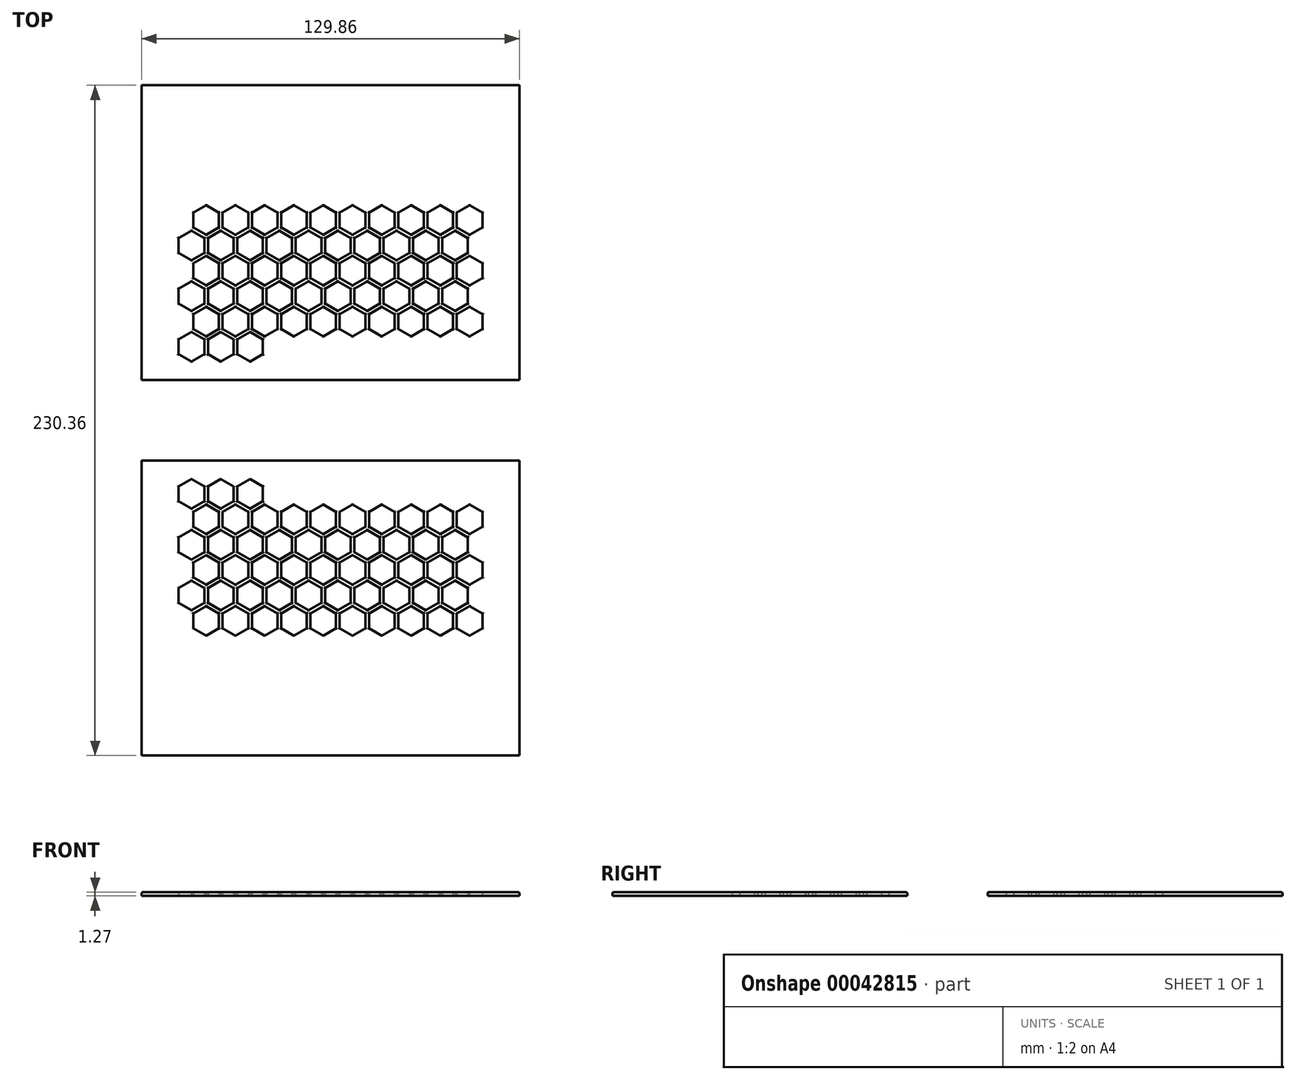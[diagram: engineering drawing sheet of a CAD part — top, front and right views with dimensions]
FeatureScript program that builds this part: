
annotation { "Feature Type Name" : "Feature", "Feature Type Description" : "" }
export const myFeature = defineFeature(function(context is Context, id is Id, definition is map)
    precondition{}
    {
        {
            var Q0;
            Q0=qCreatedBy(makeId("Top.planeOp"),FACE);
            var sketch = newSketch(context, id + "F0", { "sketchPlane" : qUnion([Q0])});
            skCircle(sketch, "E0.cCircle", {"center": v(-4.27, 25.27) * mm, "radius": 5.08 * mm, "construction": true});
            skLineSegment(sketch, "E0.0", {"start": v(-4.27, 20.19) * mm, "end": v(-8.67, 22.73) * mm});
            skLineSegment(sketch, "E0.1", {"start": v(-8.67, 22.73) * mm, "end": v(-8.67, 27.8) * mm});
            skLineSegment(sketch, "E0.2", {"start": v(-8.67, 27.8) * mm, "end": v(-4.27, 30.35) * mm});
            skLineSegment(sketch, "E0.3", {"start": v(-4.27, 30.35) * mm, "end": v(0.13, 27.8) * mm});
            skLineSegment(sketch, "E0.4", {"start": v(0.13, 27.8) * mm, "end": v(0.13, 22.73) * mm});
            skLineSegment(sketch, "E0.5", {"start": v(0.13, 22.73) * mm, "end": v(-4.27, 20.19) * mm});
            skLineSegment(sketch, "E1.1.0.0", {"start": v(5.8, 20.19) * mm, "end": v(1.4, 22.73) * mm});
            skLineSegment(sketch, "E1.1.0.1", {"start": v(1.4, 22.73) * mm, "end": v(1.4, 27.8) * mm});
            skLineSegment(sketch, "E1.1.0.2", {"start": v(1.4, 27.8) * mm, "end": v(5.8, 30.35) * mm});
            skLineSegment(sketch, "E1.1.0.3", {"start": v(5.8, 30.35) * mm, "end": v(10.2, 27.8) * mm});
            skLineSegment(sketch, "E1.1.0.4", {"start": v(10.2, 27.8) * mm, "end": v(10.2, 22.73) * mm});
            skLineSegment(sketch, "E1.1.0.5", {"start": v(10.2, 22.73) * mm, "end": v(5.8, 20.19) * mm});
            skCircle(sketch, "E1.1.0.6", {"center": v(5.8, 25.27) * mm, "radius": 5.08 * mm, "construction": true});
            skLineSegment(sketch, "E1.2.0.0", {"start": v(15.87, 20.19) * mm, "end": v(11.47, 22.73) * mm});
            skLineSegment(sketch, "E1.2.0.1", {"start": v(11.47, 22.73) * mm, "end": v(11.47, 27.8) * mm});
            skLineSegment(sketch, "E1.2.0.2", {"start": v(11.47, 27.8) * mm, "end": v(15.87, 30.35) * mm});
            skLineSegment(sketch, "E1.2.0.3", {"start": v(15.87, 30.35) * mm, "end": v(20.27, 27.8) * mm});
            skLineSegment(sketch, "E1.2.0.4", {"start": v(20.27, 27.8) * mm, "end": v(20.27, 22.73) * mm});
            skLineSegment(sketch, "E1.2.0.5", {"start": v(20.27, 22.73) * mm, "end": v(15.87, 20.19) * mm});
            skCircle(sketch, "E1.2.0.6", {"center": v(15.87, 25.27) * mm, "radius": 5.08 * mm, "construction": true});
            skLineSegment(sketch, "E1.direction1", {"start": v(-8.67, 22.73) * mm, "end": v(1.4, 22.73) * mm, "construction": true});
            skLineSegment(sketch, "E2.0.1.0", {"start": v(-3.63, 31.45) * mm, "end": v(6.44, 31.45) * mm, "construction": true});
            skLineSegment(sketch, "E2.0.1.1", {"start": v(75.65, 36.53) * mm, "end": v(75.65, 31.45) * mm});
            skLineSegment(sketch, "E2.0.1.2", {"start": v(45.44, 31.45) * mm, "end": v(41.04, 28.9) * mm});
            skLineSegment(sketch, "E2.0.1.3", {"start": v(36.64, 31.45) * mm, "end": v(36.64, 36.53) * mm});
            skCircle(sketch, "E2.0.1.4", {"center": v(61.18, 33.99) * mm, "radius": 5.08 * mm, "construction": true});
            skLineSegment(sketch, "E2.0.1.5", {"start": v(86.99, 31.45) * mm, "end": v(86.99, 36.53) * mm});
            skCircle(sketch, "E2.0.1.6", {"center": v(51.11, 33.99) * mm, "radius": 5.08 * mm, "construction": true});
            skLineSegment(sketch, "E2.0.1.7", {"start": v(5.17, 36.53) * mm, "end": v(5.17, 31.45) * mm});
            skLineSegment(sketch, "E2.0.1.8", {"start": v(46.71, 36.53) * mm, "end": v(51.11, 39.07) * mm});
            skLineSegment(sketch, "E2.0.1.9", {"start": v(61.18, 28.9) * mm, "end": v(56.78, 31.45) * mm});
            skLineSegment(sketch, "E2.0.1.10", {"start": v(26.58, 36.53) * mm, "end": v(30.98, 39.07) * mm});
            skLineSegment(sketch, "E2.0.1.11", {"start": v(55.51, 36.53) * mm, "end": v(55.51, 31.45) * mm});
            skLineSegment(sketch, "E2.0.1.12", {"start": v(81.32, 28.9) * mm, "end": v(76.92, 31.45) * mm});
            skCircle(sketch, "E2.0.1.13", {"center": v(71.25, 33.99) * mm, "radius": 5.08 * mm, "construction": true});
            skLineSegment(sketch, "E2.0.1.14", {"start": v(41.04, 28.9) * mm, "end": v(36.64, 31.45) * mm});
            skLineSegment(sketch, "E2.0.1.15", {"start": v(25.3, 31.45) * mm, "end": v(20.9, 28.9) * mm});
            skLineSegment(sketch, "E2.0.1.16", {"start": v(35.37, 36.53) * mm, "end": v(35.37, 31.45) * mm});
            skLineSegment(sketch, "E2.0.1.17", {"start": v(6.44, 36.53) * mm, "end": v(10.84, 39.07) * mm});
            skLineSegment(sketch, "E2.0.1.18", {"start": v(0.77, 28.9) * mm, "end": v(-3.63, 31.45) * mm});
            skLineSegment(sketch, "E2.0.1.19", {"start": v(41.04, 39.07) * mm, "end": v(45.44, 36.53) * mm});
            skCircle(sketch, "E2.0.1.20", {"center": v(20.9, 33.99) * mm, "radius": 5.08 * mm, "construction": true});
            skLineSegment(sketch, "E2.0.1.21", {"start": v(-3.63, 31.45) * mm, "end": v(-3.63, 36.53) * mm});
            skLineSegment(sketch, "E2.0.1.22", {"start": v(0.77, 39.07) * mm, "end": v(5.17, 36.53) * mm});
            skLineSegment(sketch, "E2.0.1.23", {"start": v(5.17, 31.45) * mm, "end": v(0.77, 28.9) * mm});
            skLineSegment(sketch, "E2.0.1.24", {"start": v(20.9, 39.07) * mm, "end": v(25.3, 36.53) * mm});
            skLineSegment(sketch, "E2.0.1.25", {"start": v(45.44, 36.53) * mm, "end": v(45.44, 31.45) * mm});
            skLineSegment(sketch, "E2.0.1.26", {"start": v(30.98, 28.9) * mm, "end": v(26.58, 31.45) * mm});
            skCircle(sketch, "E2.0.1.27", {"center": v(0.77, 33.99) * mm, "radius": 5.08 * mm, "construction": true});
            skLineSegment(sketch, "E2.0.1.28", {"start": v(71.25, 39.07) * mm, "end": v(75.65, 36.53) * mm});
            skLineSegment(sketch, "E2.0.1.29", {"start": v(65.58, 31.45) * mm, "end": v(61.18, 28.9) * mm});
            skLineSegment(sketch, "E2.0.1.30", {"start": v(56.78, 31.45) * mm, "end": v(56.78, 36.53) * mm});
            skLineSegment(sketch, "E2.0.1.31", {"start": v(36.64, 36.53) * mm, "end": v(41.04, 39.07) * mm});
            skLineSegment(sketch, "E2.0.1.32", {"start": v(66.85, 31.45) * mm, "end": v(66.85, 36.53) * mm});
            skLineSegment(sketch, "E2.0.1.33", {"start": v(-3.63, 36.53) * mm, "end": v(0.77, 39.07) * mm});
            skCircle(sketch, "E2.0.1.34", {"center": v(10.84, 33.99) * mm, "radius": 5.08 * mm, "construction": true});
            skLineSegment(sketch, "E2.0.1.35", {"start": v(16.5, 36.53) * mm, "end": v(20.9, 39.07) * mm});
            skLineSegment(sketch, "E2.0.1.36", {"start": v(85.72, 31.45) * mm, "end": v(81.32, 28.9) * mm});
            skLineSegment(sketch, "E2.0.1.37", {"start": v(10.84, 39.07) * mm, "end": v(15.24, 36.53) * mm});
            skLineSegment(sketch, "E2.0.1.38", {"start": v(65.58, 36.53) * mm, "end": v(65.58, 31.45) * mm});
            skLineSegment(sketch, "E2.0.1.39", {"start": v(81.32, 39.07) * mm, "end": v(85.72, 36.53) * mm});
            skLineSegment(sketch, "E2.0.1.40", {"start": v(10.84, 28.9) * mm, "end": v(6.44, 31.45) * mm});
            skLineSegment(sketch, "E2.0.1.41", {"start": v(26.58, 31.45) * mm, "end": v(26.58, 36.53) * mm});
            skLineSegment(sketch, "E2.0.1.42", {"start": v(51.11, 39.07) * mm, "end": v(55.51, 36.53) * mm});
            skCircle(sketch, "E2.0.1.43", {"center": v(41.04, 33.99) * mm, "radius": 5.08 * mm, "construction": true});
            skLineSegment(sketch, "E2.0.1.44", {"start": v(56.78, 36.53) * mm, "end": v(61.18, 39.07) * mm});
            skCircle(sketch, "E2.0.1.45", {"center": v(91.39, 33.99) * mm, "radius": 5.08 * mm, "construction": true});
            skLineSegment(sketch, "E2.0.1.46", {"start": v(6.44, 31.45) * mm, "end": v(6.44, 36.53) * mm});
            skLineSegment(sketch, "E2.0.1.47", {"start": v(35.37, 31.45) * mm, "end": v(30.98, 28.9) * mm});
            skLineSegment(sketch, "E2.0.1.48", {"start": v(16.5, 31.45) * mm, "end": v(16.5, 36.53) * mm});
            skLineSegment(sketch, "E2.0.1.49", {"start": v(91.39, 28.9) * mm, "end": v(86.99, 31.45) * mm});
            skCircle(sketch, "E2.0.1.50", {"center": v(30.98, 33.99) * mm, "radius": 5.08 * mm, "construction": true});
            skLineSegment(sketch, "E2.0.1.51", {"start": v(91.39, 39.07) * mm, "end": v(95.79, 36.53) * mm});
            skLineSegment(sketch, "E2.0.1.52", {"start": v(95.79, 31.45) * mm, "end": v(91.39, 28.9) * mm});
            skLineSegment(sketch, "E2.0.1.53", {"start": v(86.99, 36.53) * mm, "end": v(91.39, 39.07) * mm});
            skLineSegment(sketch, "E2.0.1.54", {"start": v(95.79, 36.53) * mm, "end": v(95.79, 31.45) * mm});
            skLineSegment(sketch, "E2.0.1.55", {"start": v(55.51, 31.45) * mm, "end": v(51.11, 28.9) * mm});
            skLineSegment(sketch, "E2.0.1.56", {"start": v(30.98, 39.07) * mm, "end": v(35.37, 36.53) * mm});
            skLineSegment(sketch, "E2.0.1.57", {"start": v(25.3, 36.53) * mm, "end": v(25.3, 31.45) * mm});
            skLineSegment(sketch, "E2.0.1.58", {"start": v(76.92, 31.45) * mm, "end": v(76.92, 36.53) * mm});
            skCircle(sketch, "E2.0.1.59", {"center": v(81.32, 33.99) * mm, "radius": 5.08 * mm, "construction": true});
            skLineSegment(sketch, "E2.0.1.60", {"start": v(85.72, 36.53) * mm, "end": v(85.72, 31.45) * mm});
            skLineSegment(sketch, "E2.0.1.61", {"start": v(71.25, 28.9) * mm, "end": v(66.85, 31.45) * mm});
            skLineSegment(sketch, "E2.0.1.62", {"start": v(61.18, 39.07) * mm, "end": v(65.58, 36.53) * mm});
            skLineSegment(sketch, "E2.0.1.63", {"start": v(66.85, 36.53) * mm, "end": v(71.25, 39.07) * mm});
            skLineSegment(sketch, "E2.0.1.64", {"start": v(15.24, 36.53) * mm, "end": v(15.24, 31.45) * mm});
            skLineSegment(sketch, "E2.0.1.65", {"start": v(15.24, 31.45) * mm, "end": v(10.84, 28.9) * mm});
            skLineSegment(sketch, "E2.0.1.66", {"start": v(51.11, 28.9) * mm, "end": v(46.71, 31.45) * mm});
            skLineSegment(sketch, "E2.0.1.67", {"start": v(46.71, 31.45) * mm, "end": v(46.71, 36.53) * mm});
            skLineSegment(sketch, "E2.0.1.68", {"start": v(76.92, 36.53) * mm, "end": v(81.32, 39.07) * mm});
            skLineSegment(sketch, "E2.0.1.69", {"start": v(20.9, 28.9) * mm, "end": v(16.5, 31.45) * mm});
            skLineSegment(sketch, "E2.0.1.70", {"start": v(75.65, 31.45) * mm, "end": v(71.25, 28.9) * mm});
            skLineSegment(sketch, "E2.direction1", {"start": v(-8.67, 22.73) * mm, "end": v(18.3, 22.73) * mm, "construction": true});
            skLineSegment(sketch, "E2.direction2", {"start": v(-8.67, 22.73) * mm, "end": v(-3.63, 31.45) * mm, "construction": true});
            skLineSegment(sketch, "E3", {"start": v(0.13, 27.8) * mm, "end": v(0.77, 28.9) * mm, "construction": true});
            skLineSegment(sketch, "E4", {"start": v(0.77, 28.9) * mm, "end": v(1.4, 27.8) * mm, "construction": true});
            skLineSegment(sketch, "E5", {"start": v(0.13, 27.8) * mm, "end": v(1.4, 27.8) * mm, "construction": true});
            skLineSegment(sketch, "E6.0.1.0", {"start": v(-3.63, 48.89) * mm, "end": v(6.44, 48.89) * mm, "construction": true});
            skCircle(sketch, "E6.0.1.1", {"center": v(20.9, 51.43) * mm, "radius": 5.08 * mm, "construction": true});
            skLineSegment(sketch, "E6.0.1.2", {"start": v(76.92, 53.97) * mm, "end": v(81.32, 56.5) * mm});
            skCircle(sketch, "E6.0.1.3", {"center": v(61.18, 51.43) * mm, "radius": 5.08 * mm, "construction": true});
            skLineSegment(sketch, "E6.0.1.4", {"start": v(80.68, 45.25) * mm, "end": v(80.68, 40.17) * mm});
            skLineSegment(sketch, "E6.0.1.5", {"start": v(-8.67, 40.17) * mm, "end": v(18.3, 40.17) * mm, "construction": true});
            skCircle(sketch, "E6.0.1.6", {"center": v(51.11, 51.43) * mm, "radius": 5.08 * mm, "construction": true});
            skCircle(sketch, "E6.0.1.7", {"center": v(0.77, 51.43) * mm, "radius": 5.08 * mm, "construction": true});
            skLineSegment(sketch, "E6.0.1.8", {"start": v(61.82, 40.17) * mm, "end": v(61.82, 45.25) * mm});
            skCircle(sketch, "E6.0.1.9", {"center": v(76.28, 42.7) * mm, "radius": 5.08 * mm, "construction": true});
            skLineSegment(sketch, "E6.0.1.10", {"start": v(56.15, 37.63) * mm, "end": v(51.75, 40.17) * mm});
            skLineSegment(sketch, "E6.0.1.11", {"start": v(15.87, 37.63) * mm, "end": v(11.47, 40.17) * mm});
            skLineSegment(sketch, "E6.0.1.12", {"start": v(71.25, 56.5) * mm, "end": v(75.65, 53.97) * mm});
            skLineSegment(sketch, "E6.0.1.13", {"start": v(20.27, 40.17) * mm, "end": v(15.87, 37.63) * mm});
            skLineSegment(sketch, "E6.0.1.14", {"start": v(56.78, 53.97) * mm, "end": v(61.18, 56.5) * mm});
            skLineSegment(sketch, "E6.0.1.15", {"start": v(95.79, 48.89) * mm, "end": v(91.39, 46.35) * mm});
            skLineSegment(sketch, "E6.0.1.16", {"start": v(30.34, 40.17) * mm, "end": v(25.94, 37.63) * mm});
            skLineSegment(sketch, "E6.0.1.17", {"start": v(60.55, 45.25) * mm, "end": v(60.55, 40.17) * mm});
            skLineSegment(sketch, "E6.0.1.18", {"start": v(91.39, 56.5) * mm, "end": v(95.79, 53.97) * mm});
            skLineSegment(sketch, "E6.0.1.19", {"start": v(-8.67, 40.17) * mm, "end": v(-3.63, 48.89) * mm, "construction": true});
            skLineSegment(sketch, "E6.0.1.20", {"start": v(41.04, 56.5) * mm, "end": v(45.44, 53.97) * mm});
            skLineSegment(sketch, "E6.0.1.21", {"start": v(36, 37.63) * mm, "end": v(31.61, 40.17) * mm});
            skLineSegment(sketch, "E6.0.1.22", {"start": v(81.32, 56.5) * mm, "end": v(85.72, 53.97) * mm});
            skLineSegment(sketch, "E6.0.1.23", {"start": v(66.22, 37.63) * mm, "end": v(61.82, 40.17) * mm});
            skLineSegment(sketch, "E6.0.1.24", {"start": v(40.4, 40.17) * mm, "end": v(36, 37.63) * mm});
            skLineSegment(sketch, "E6.0.1.25", {"start": v(10.84, 56.5) * mm, "end": v(15.24, 53.97) * mm});
            skLineSegment(sketch, "E6.0.1.26", {"start": v(55.51, 53.97) * mm, "end": v(55.51, 48.89) * mm});
            skLineSegment(sketch, "E6.0.1.27", {"start": v(61.18, 46.35) * mm, "end": v(56.78, 48.89) * mm});
            skLineSegment(sketch, "E6.0.1.28", {"start": v(60.55, 40.17) * mm, "end": v(56.15, 37.63) * mm});
            skLineSegment(sketch, "E6.0.1.29", {"start": v(10.2, 40.17) * mm, "end": v(5.8, 37.63) * mm});
            skLineSegment(sketch, "E6.0.1.30", {"start": v(0.13, 40.17) * mm, "end": v(-4.27, 37.63) * mm});
            skLineSegment(sketch, "E6.0.1.31", {"start": v(45.44, 53.97) * mm, "end": v(45.44, 48.89) * mm});
            skCircle(sketch, "E6.0.1.32", {"center": v(10.84, 51.43) * mm, "radius": 5.08 * mm, "construction": true});
            skLineSegment(sketch, "E6.0.1.33", {"start": v(65.58, 53.97) * mm, "end": v(65.58, 48.89) * mm});
            skLineSegment(sketch, "E6.0.1.34", {"start": v(-3.63, 48.89) * mm, "end": v(-3.63, 53.97) * mm});
            skCircle(sketch, "E6.0.1.35", {"center": v(71.25, 51.43) * mm, "radius": 5.08 * mm, "construction": true});
            skLineSegment(sketch, "E6.0.1.36", {"start": v(90.75, 45.25) * mm, "end": v(90.75, 40.17) * mm});
            skLineSegment(sketch, "E6.0.1.37", {"start": v(61.82, 45.25) * mm, "end": v(66.22, 47.79) * mm});
            skLineSegment(sketch, "E6.0.1.38", {"start": v(46.08, 37.63) * mm, "end": v(41.68, 40.17) * mm});
            skLineSegment(sketch, "E6.0.1.39", {"start": v(71.25, 46.35) * mm, "end": v(66.85, 48.89) * mm});
            skCircle(sketch, "E6.0.1.40", {"center": v(91.39, 51.43) * mm, "radius": 5.08 * mm, "construction": true});
            skLineSegment(sketch, "E6.0.1.41", {"start": v(65.58, 48.89) * mm, "end": v(61.18, 46.35) * mm});
            skLineSegment(sketch, "E6.0.1.42", {"start": v(20.9, 56.5) * mm, "end": v(25.3, 53.97) * mm});
            skLineSegment(sketch, "E6.0.1.43", {"start": v(56.15, 47.79) * mm, "end": v(60.55, 45.25) * mm});
            skLineSegment(sketch, "E6.0.1.44", {"start": v(-8.67, 45.25) * mm, "end": v(-4.27, 47.79) * mm});
            skCircle(sketch, "E6.0.1.45", {"center": v(25.94, 42.7) * mm, "radius": 5.08 * mm, "construction": true});
            skLineSegment(sketch, "E6.0.1.46", {"start": v(90.75, 40.17) * mm, "end": v(86.35, 37.63) * mm});
            skCircle(sketch, "E6.0.1.47", {"center": v(-4.27, 42.7) * mm, "radius": 5.08 * mm, "construction": true});
            skLineSegment(sketch, "E6.0.1.48", {"start": v(51.11, 56.5) * mm, "end": v(55.51, 53.97) * mm});
            skLineSegment(sketch, "E6.0.1.49", {"start": v(80.68, 40.17) * mm, "end": v(76.28, 37.63) * mm});
            skCircle(sketch, "E6.0.1.50", {"center": v(5.8, 42.7) * mm, "radius": 5.08 * mm, "construction": true});
            skLineSegment(sketch, "E6.0.1.51", {"start": v(0.77, 56.5) * mm, "end": v(5.17, 53.97) * mm});
            skLineSegment(sketch, "E6.0.1.52", {"start": v(66.22, 47.79) * mm, "end": v(70.62, 45.25) * mm});
            skLineSegment(sketch, "E6.0.1.53", {"start": v(61.18, 56.5) * mm, "end": v(65.58, 53.97) * mm});
            skLineSegment(sketch, "E6.0.1.54", {"start": v(56.78, 48.89) * mm, "end": v(56.78, 53.97) * mm});
            skLineSegment(sketch, "E6.0.1.55", {"start": v(81.95, 40.17) * mm, "end": v(81.95, 45.25) * mm});
            skCircle(sketch, "E6.0.1.56", {"center": v(56.15, 42.7) * mm, "radius": 5.08 * mm, "construction": true});
            skLineSegment(sketch, "E6.0.1.57", {"start": v(86.99, 53.97) * mm, "end": v(91.39, 56.5) * mm});
            skCircle(sketch, "E6.0.1.58", {"center": v(81.32, 51.43) * mm, "radius": 5.08 * mm, "construction": true});
            skLineSegment(sketch, "E6.0.1.59", {"start": v(-4.27, 37.63) * mm, "end": v(-8.67, 40.17) * mm});
            skLineSegment(sketch, "E6.0.1.60", {"start": v(25.94, 37.63) * mm, "end": v(21.54, 40.17) * mm});
            skCircle(sketch, "E6.0.1.61", {"center": v(86.35, 42.7) * mm, "radius": 5.08 * mm, "construction": true});
            skLineSegment(sketch, "E6.0.1.62", {"start": v(41.68, 45.25) * mm, "end": v(46.08, 47.79) * mm});
            skLineSegment(sketch, "E6.0.1.63", {"start": v(66.85, 53.97) * mm, "end": v(71.25, 56.5) * mm});
            skLineSegment(sketch, "E6.0.1.64", {"start": v(36.64, 53.97) * mm, "end": v(41.04, 56.5) * mm});
            skLineSegment(sketch, "E6.0.1.65", {"start": v(70.62, 40.17) * mm, "end": v(66.22, 37.63) * mm});
            skLineSegment(sketch, "E6.0.1.66", {"start": v(16.5, 48.89) * mm, "end": v(16.5, 53.97) * mm});
            skLineSegment(sketch, "E6.0.1.67", {"start": v(66.85, 48.89) * mm, "end": v(66.85, 53.97) * mm});
            skLineSegment(sketch, "E6.0.1.68", {"start": v(15.24, 53.97) * mm, "end": v(15.24, 48.89) * mm});
            skCircle(sketch, "E6.0.1.69", {"center": v(66.22, 42.7) * mm, "radius": 5.08 * mm, "construction": true});
            skLineSegment(sketch, "E6.0.1.70", {"start": v(50.48, 45.25) * mm, "end": v(50.48, 40.17) * mm});
            skLineSegment(sketch, "E6.0.1.71", {"start": v(-3.63, 53.97) * mm, "end": v(0.77, 56.5) * mm});
            skLineSegment(sketch, "E6.0.1.72", {"start": v(6.44, 53.97) * mm, "end": v(10.84, 56.5) * mm});
            skLineSegment(sketch, "E6.0.1.73", {"start": v(-8.67, 40.17) * mm, "end": v(-8.67, 45.25) * mm});
            skCircle(sketch, "E6.0.1.74", {"center": v(41.04, 51.43) * mm, "radius": 5.08 * mm, "construction": true});
            skLineSegment(sketch, "E6.0.1.75", {"start": v(46.71, 48.89) * mm, "end": v(46.71, 53.97) * mm});
            skLineSegment(sketch, "E6.0.1.76", {"start": v(16.5, 53.97) * mm, "end": v(20.9, 56.5) * mm});
            skLineSegment(sketch, "E6.0.1.77", {"start": v(5.8, 37.63) * mm, "end": v(1.4, 40.17) * mm});
            skLineSegment(sketch, "E6.0.1.78", {"start": v(30.98, 56.5) * mm, "end": v(35.37, 53.97) * mm});
            skCircle(sketch, "E6.0.1.79", {"center": v(46.08, 42.7) * mm, "radius": 5.08 * mm, "construction": true});
            skLineSegment(sketch, "E6.0.1.80", {"start": v(86.35, 37.63) * mm, "end": v(81.95, 40.17) * mm});
            skLineSegment(sketch, "E6.0.1.81", {"start": v(95.79, 53.97) * mm, "end": v(95.79, 48.89) * mm});
            skLineSegment(sketch, "E6.0.1.82", {"start": v(51.75, 40.17) * mm, "end": v(51.75, 45.25) * mm});
            skLineSegment(sketch, "E6.0.1.83", {"start": v(46.71, 53.97) * mm, "end": v(51.11, 56.5) * mm});
            skCircle(sketch, "E6.0.1.84", {"center": v(30.98, 51.43) * mm, "radius": 5.08 * mm, "construction": true});
            skLineSegment(sketch, "E6.0.1.85", {"start": v(26.58, 53.97) * mm, "end": v(30.98, 56.5) * mm});
            skLineSegment(sketch, "E6.0.1.86", {"start": v(50.48, 40.17) * mm, "end": v(46.08, 37.63) * mm});
            skLineSegment(sketch, "E6.0.1.87", {"start": v(76.28, 37.63) * mm, "end": v(71.89, 40.17) * mm});
            skLineSegment(sketch, "E6.0.1.88", {"start": v(5.17, 53.97) * mm, "end": v(5.17, 48.89) * mm});
            skLineSegment(sketch, "E6.0.1.89", {"start": v(51.11, 46.35) * mm, "end": v(46.71, 48.89) * mm});
            skLineSegment(sketch, "E6.0.1.90", {"start": v(86.35, 47.79) * mm, "end": v(90.75, 45.25) * mm});
            skLineSegment(sketch, "E6.0.1.91", {"start": v(71.89, 40.17) * mm, "end": v(71.89, 45.25) * mm});
            skLineSegment(sketch, "E6.0.1.92", {"start": v(81.32, 46.35) * mm, "end": v(76.92, 48.89) * mm});
            skCircle(sketch, "E6.0.1.93", {"center": v(36, 42.7) * mm, "radius": 5.08 * mm, "construction": true});
            skLineSegment(sketch, "E6.0.1.94", {"start": v(85.72, 53.97) * mm, "end": v(85.72, 48.89) * mm});
            skLineSegment(sketch, "E6.0.1.95", {"start": v(10.84, 46.35) * mm, "end": v(6.44, 48.89) * mm});
            skLineSegment(sketch, "E6.0.1.96", {"start": v(20.27, 45.25) * mm, "end": v(20.27, 40.17) * mm});
            skLineSegment(sketch, "E6.0.1.97", {"start": v(31.61, 40.17) * mm, "end": v(31.61, 45.25) * mm});
            skLineSegment(sketch, "E6.0.1.98", {"start": v(30.34, 45.25) * mm, "end": v(30.34, 40.17) * mm});
            skLineSegment(sketch, "E6.0.1.99", {"start": v(5.17, 48.89) * mm, "end": v(0.77, 46.35) * mm});
            skLineSegment(sketch, "E6.0.1.100", {"start": v(31.61, 45.25) * mm, "end": v(36, 47.79) * mm});
            skLineSegment(sketch, "E6.0.1.101", {"start": v(81.95, 45.25) * mm, "end": v(86.35, 47.79) * mm});
            skLineSegment(sketch, "E6.0.1.102", {"start": v(86.99, 48.89) * mm, "end": v(86.99, 53.97) * mm});
            skLineSegment(sketch, "E6.0.1.103", {"start": v(55.51, 48.89) * mm, "end": v(51.11, 46.35) * mm});
            skLineSegment(sketch, "E6.0.1.104", {"start": v(75.65, 48.89) * mm, "end": v(71.25, 46.35) * mm});
            skLineSegment(sketch, "E6.0.1.105", {"start": v(76.28, 47.79) * mm, "end": v(80.68, 45.25) * mm});
            skLineSegment(sketch, "E6.0.1.106", {"start": v(30.98, 46.35) * mm, "end": v(26.58, 48.89) * mm});
            skLineSegment(sketch, "E6.0.1.107", {"start": v(26.58, 48.89) * mm, "end": v(26.58, 53.97) * mm});
            skLineSegment(sketch, "E6.0.1.108", {"start": v(1.4, 45.25) * mm, "end": v(5.8, 47.79) * mm});
            skLineSegment(sketch, "E6.0.1.109", {"start": v(15.87, 47.79) * mm, "end": v(20.27, 45.25) * mm});
            skLineSegment(sketch, "E6.0.1.110", {"start": v(45.44, 48.89) * mm, "end": v(41.04, 46.35) * mm});
            skLineSegment(sketch, "E6.0.1.111", {"start": v(76.92, 48.89) * mm, "end": v(76.92, 53.97) * mm});
            skLineSegment(sketch, "E6.0.1.112", {"start": v(1.4, 40.17) * mm, "end": v(1.4, 45.25) * mm});
            skLineSegment(sketch, "E6.0.1.113", {"start": v(10.2, 45.25) * mm, "end": v(10.2, 40.17) * mm});
            skLineSegment(sketch, "E6.0.1.114", {"start": v(20.9, 46.35) * mm, "end": v(16.5, 48.89) * mm});
            skLineSegment(sketch, "E6.0.1.115", {"start": v(25.3, 53.97) * mm, "end": v(25.3, 48.89) * mm});
            skCircle(sketch, "E6.0.1.116", {"center": v(15.87, 42.7) * mm, "radius": 5.08 * mm, "construction": true});
            skLineSegment(sketch, "E6.0.1.117", {"start": v(0.13, 45.25) * mm, "end": v(0.13, 40.17) * mm});
            skLineSegment(sketch, "E6.0.1.118", {"start": v(36, 47.79) * mm, "end": v(40.4, 45.25) * mm});
            skLineSegment(sketch, "E6.0.1.119", {"start": v(-8.67, 40.17) * mm, "end": v(1.4, 40.17) * mm, "construction": true});
            skLineSegment(sketch, "E6.0.1.120", {"start": v(41.04, 46.35) * mm, "end": v(36.64, 48.89) * mm});
            skLineSegment(sketch, "E6.0.1.121", {"start": v(11.47, 45.25) * mm, "end": v(15.87, 47.79) * mm});
            skLineSegment(sketch, "E6.0.1.122", {"start": v(41.68, 40.17) * mm, "end": v(41.68, 45.25) * mm});
            skLineSegment(sketch, "E6.0.1.123", {"start": v(6.44, 48.89) * mm, "end": v(6.44, 53.97) * mm});
            skLineSegment(sketch, "E6.0.1.124", {"start": v(51.75, 45.25) * mm, "end": v(56.15, 47.79) * mm});
            skLineSegment(sketch, "E6.0.1.125", {"start": v(40.4, 45.25) * mm, "end": v(40.4, 40.17) * mm});
            skLineSegment(sketch, "E6.0.1.126", {"start": v(25.3, 48.89) * mm, "end": v(20.9, 46.35) * mm});
            skLineSegment(sketch, "E6.0.1.127", {"start": v(70.62, 45.25) * mm, "end": v(70.62, 40.17) * mm});
            skLineSegment(sketch, "E6.0.1.128", {"start": v(35.37, 48.89) * mm, "end": v(30.98, 46.35) * mm});
            skLineSegment(sketch, "E6.0.1.129", {"start": v(46.08, 47.79) * mm, "end": v(50.48, 45.25) * mm});
            skLineSegment(sketch, "E6.0.1.130", {"start": v(21.54, 40.17) * mm, "end": v(21.54, 45.25) * mm});
            skLineSegment(sketch, "E6.0.1.131", {"start": v(35.37, 53.97) * mm, "end": v(35.37, 48.89) * mm});
            skLineSegment(sketch, "E6.0.1.132", {"start": v(85.72, 48.89) * mm, "end": v(81.32, 46.35) * mm});
            skLineSegment(sketch, "E6.0.1.133", {"start": v(71.89, 45.25) * mm, "end": v(76.28, 47.79) * mm});
            skLineSegment(sketch, "E6.0.1.134", {"start": v(21.54, 45.25) * mm, "end": v(25.94, 47.79) * mm});
            skLineSegment(sketch, "E6.0.1.135", {"start": v(91.39, 46.35) * mm, "end": v(86.99, 48.89) * mm});
            skLineSegment(sketch, "E6.0.1.136", {"start": v(75.65, 53.97) * mm, "end": v(75.65, 48.89) * mm});
            skLineSegment(sketch, "E6.0.1.137", {"start": v(15.24, 48.89) * mm, "end": v(10.84, 46.35) * mm});
            skLineSegment(sketch, "E6.0.1.138", {"start": v(36.64, 48.89) * mm, "end": v(36.64, 53.97) * mm});
            skLineSegment(sketch, "E6.0.1.139", {"start": v(5.8, 47.79) * mm, "end": v(10.2, 45.25) * mm});
            skLineSegment(sketch, "E6.0.1.140", {"start": v(25.94, 47.79) * mm, "end": v(30.34, 45.25) * mm});
            skLineSegment(sketch, "E6.0.1.141", {"start": v(11.47, 40.17) * mm, "end": v(11.47, 45.25) * mm});
            skLineSegment(sketch, "E6.0.1.142", {"start": v(0.77, 46.35) * mm, "end": v(1.4, 45.25) * mm, "construction": true});
            skLineSegment(sketch, "E6.0.1.143", {"start": v(-4.27, 47.79) * mm, "end": v(0.13, 45.25) * mm});
            skLineSegment(sketch, "E6.0.1.144", {"start": v(0.77, 46.35) * mm, "end": v(-3.63, 48.89) * mm});
            skLineSegment(sketch, "E6.0.1.145", {"start": v(0.13, 45.25) * mm, "end": v(1.4, 45.25) * mm, "construction": true});
            skLineSegment(sketch, "E6.0.1.146", {"start": v(0.13, 45.25) * mm, "end": v(0.77, 46.35) * mm, "construction": true});
            skLineSegment(sketch, "E6.0.2.0", {"start": v(-3.63, 66.33) * mm, "end": v(6.44, 66.33) * mm, "construction": true});
            skCircle(sketch, "E6.0.2.1", {"center": v(20.9, 68.87) * mm, "radius": 5.08 * mm, "construction": true});
            skLineSegment(sketch, "E6.0.2.2", {"start": v(76.92, 71.4) * mm, "end": v(81.32, 73.95) * mm});
            skCircle(sketch, "E6.0.2.3", {"center": v(61.18, 68.87) * mm, "radius": 5.08 * mm, "construction": true});
            skLineSegment(sketch, "E6.0.2.4", {"start": v(80.68, 62.69) * mm, "end": v(80.68, 57.6) * mm});
            skLineSegment(sketch, "E6.0.2.5", {"start": v(-8.67, 57.6) * mm, "end": v(18.3, 57.6) * mm, "construction": true});
            skCircle(sketch, "E6.0.2.6", {"center": v(51.11, 68.87) * mm, "radius": 5.08 * mm, "construction": true});
            skCircle(sketch, "E6.0.2.7", {"center": v(0.77, 68.87) * mm, "radius": 5.08 * mm, "construction": true});
            skLineSegment(sketch, "E6.0.2.8", {"start": v(61.82, 57.6) * mm, "end": v(61.82, 62.69) * mm});
            skCircle(sketch, "E6.0.2.9", {"center": v(76.28, 60.15) * mm, "radius": 5.08 * mm, "construction": true});
            skLineSegment(sketch, "E6.0.2.10", {"start": v(56.15, 55.07) * mm, "end": v(51.75, 57.6) * mm});
            skLineSegment(sketch, "E6.0.2.11", {"start": v(15.87, 55.07) * mm, "end": v(11.47, 57.6) * mm});
            skLineSegment(sketch, "E6.0.2.12", {"start": v(71.25, 73.95) * mm, "end": v(75.65, 71.4) * mm});
            skLineSegment(sketch, "E6.0.2.13", {"start": v(20.27, 57.6) * mm, "end": v(15.87, 55.07) * mm});
            skLineSegment(sketch, "E6.0.2.14", {"start": v(56.78, 71.4) * mm, "end": v(61.18, 73.95) * mm});
            skLineSegment(sketch, "E6.0.2.15", {"start": v(95.79, 66.33) * mm, "end": v(91.39, 63.79) * mm});
            skLineSegment(sketch, "E6.0.2.16", {"start": v(30.34, 57.6) * mm, "end": v(25.94, 55.07) * mm});
            skLineSegment(sketch, "E6.0.2.17", {"start": v(60.55, 62.69) * mm, "end": v(60.55, 57.6) * mm});
            skLineSegment(sketch, "E6.0.2.18", {"start": v(91.39, 73.95) * mm, "end": v(95.79, 71.4) * mm});
            skLineSegment(sketch, "E6.0.2.19", {"start": v(-8.67, 57.6) * mm, "end": v(-3.63, 66.33) * mm, "construction": true});
            skLineSegment(sketch, "E6.0.2.20", {"start": v(41.04, 73.95) * mm, "end": v(45.44, 71.4) * mm});
            skLineSegment(sketch, "E6.0.2.21", {"start": v(36, 55.07) * mm, "end": v(31.61, 57.6) * mm});
            skLineSegment(sketch, "E6.0.2.22", {"start": v(81.32, 73.95) * mm, "end": v(85.72, 71.4) * mm});
            skLineSegment(sketch, "E6.0.2.23", {"start": v(66.22, 55.07) * mm, "end": v(61.82, 57.6) * mm});
            skLineSegment(sketch, "E6.0.2.24", {"start": v(40.4, 57.6) * mm, "end": v(36, 55.07) * mm});
            skLineSegment(sketch, "E6.0.2.25", {"start": v(10.84, 73.95) * mm, "end": v(15.24, 71.4) * mm});
            skLineSegment(sketch, "E6.0.2.26", {"start": v(55.51, 71.4) * mm, "end": v(55.51, 66.33) * mm});
            skLineSegment(sketch, "E6.0.2.27", {"start": v(61.18, 63.79) * mm, "end": v(56.78, 66.33) * mm});
            skLineSegment(sketch, "E6.0.2.28", {"start": v(60.55, 57.6) * mm, "end": v(56.15, 55.07) * mm});
            skLineSegment(sketch, "E6.0.2.29", {"start": v(10.2, 57.6) * mm, "end": v(5.8, 55.07) * mm});
            skLineSegment(sketch, "E6.0.2.30", {"start": v(0.13, 57.6) * mm, "end": v(-4.27, 55.07) * mm});
            skLineSegment(sketch, "E6.0.2.31", {"start": v(45.44, 71.4) * mm, "end": v(45.44, 66.33) * mm});
            skCircle(sketch, "E6.0.2.32", {"center": v(10.84, 68.87) * mm, "radius": 5.08 * mm, "construction": true});
            skLineSegment(sketch, "E6.0.2.33", {"start": v(65.58, 71.4) * mm, "end": v(65.58, 66.33) * mm});
            skLineSegment(sketch, "E6.0.2.34", {"start": v(-3.63, 66.33) * mm, "end": v(-3.63, 71.4) * mm});
            skCircle(sketch, "E6.0.2.35", {"center": v(71.25, 68.87) * mm, "radius": 5.08 * mm, "construction": true});
            skLineSegment(sketch, "E6.0.2.36", {"start": v(90.75, 62.69) * mm, "end": v(90.75, 57.6) * mm});
            skLineSegment(sketch, "E6.0.2.37", {"start": v(61.82, 62.69) * mm, "end": v(66.22, 65.23) * mm});
            skLineSegment(sketch, "E6.0.2.38", {"start": v(46.08, 55.07) * mm, "end": v(41.68, 57.6) * mm});
            skLineSegment(sketch, "E6.0.2.39", {"start": v(71.25, 63.79) * mm, "end": v(66.85, 66.33) * mm});
            skCircle(sketch, "E6.0.2.40", {"center": v(91.39, 68.87) * mm, "radius": 5.08 * mm, "construction": true});
            skLineSegment(sketch, "E6.0.2.41", {"start": v(65.58, 66.33) * mm, "end": v(61.18, 63.79) * mm});
            skLineSegment(sketch, "E6.0.2.42", {"start": v(20.9, 73.95) * mm, "end": v(25.3, 71.4) * mm});
            skLineSegment(sketch, "E6.0.2.43", {"start": v(56.15, 65.23) * mm, "end": v(60.55, 62.69) * mm});
            skLineSegment(sketch, "E6.0.2.44", {"start": v(-8.67, 62.69) * mm, "end": v(-4.27, 65.23) * mm});
            skCircle(sketch, "E6.0.2.45", {"center": v(25.94, 60.15) * mm, "radius": 5.08 * mm, "construction": true});
            skLineSegment(sketch, "E6.0.2.46", {"start": v(90.75, 57.6) * mm, "end": v(86.35, 55.07) * mm});
            skCircle(sketch, "E6.0.2.47", {"center": v(-4.27, 60.15) * mm, "radius": 5.08 * mm, "construction": true});
            skLineSegment(sketch, "E6.0.2.48", {"start": v(51.11, 73.95) * mm, "end": v(55.51, 71.4) * mm});
            skLineSegment(sketch, "E6.0.2.49", {"start": v(80.68, 57.6) * mm, "end": v(76.28, 55.07) * mm});
            skCircle(sketch, "E6.0.2.50", {"center": v(5.8, 60.15) * mm, "radius": 5.08 * mm, "construction": true});
            skLineSegment(sketch, "E6.0.2.51", {"start": v(0.77, 73.95) * mm, "end": v(5.17, 71.4) * mm});
            skLineSegment(sketch, "E6.0.2.52", {"start": v(66.22, 65.23) * mm, "end": v(70.62, 62.69) * mm});
            skLineSegment(sketch, "E6.0.2.53", {"start": v(61.18, 73.95) * mm, "end": v(65.58, 71.4) * mm});
            skLineSegment(sketch, "E6.0.2.54", {"start": v(56.78, 66.33) * mm, "end": v(56.78, 71.4) * mm});
            skLineSegment(sketch, "E6.0.2.55", {"start": v(81.95, 57.6) * mm, "end": v(81.95, 62.69) * mm});
            skCircle(sketch, "E6.0.2.56", {"center": v(56.15, 60.15) * mm, "radius": 5.08 * mm, "construction": true});
            skLineSegment(sketch, "E6.0.2.57", {"start": v(86.99, 71.4) * mm, "end": v(91.39, 73.95) * mm});
            skCircle(sketch, "E6.0.2.58", {"center": v(81.32, 68.87) * mm, "radius": 5.08 * mm, "construction": true});
            skLineSegment(sketch, "E6.0.2.59", {"start": v(-4.27, 55.07) * mm, "end": v(-8.67, 57.6) * mm});
            skLineSegment(sketch, "E6.0.2.60", {"start": v(25.94, 55.07) * mm, "end": v(21.54, 57.6) * mm});
            skCircle(sketch, "E6.0.2.61", {"center": v(86.35, 60.15) * mm, "radius": 5.08 * mm, "construction": true});
            skLineSegment(sketch, "E6.0.2.62", {"start": v(41.68, 62.69) * mm, "end": v(46.08, 65.23) * mm});
            skLineSegment(sketch, "E6.0.2.63", {"start": v(66.85, 71.4) * mm, "end": v(71.25, 73.95) * mm});
            skLineSegment(sketch, "E6.0.2.64", {"start": v(36.64, 71.4) * mm, "end": v(41.04, 73.95) * mm});
            skLineSegment(sketch, "E6.0.2.65", {"start": v(70.62, 57.6) * mm, "end": v(66.22, 55.07) * mm});
            skLineSegment(sketch, "E6.0.2.66", {"start": v(16.5, 66.33) * mm, "end": v(16.5, 71.4) * mm});
            skLineSegment(sketch, "E6.0.2.67", {"start": v(66.85, 66.33) * mm, "end": v(66.85, 71.4) * mm});
            skLineSegment(sketch, "E6.0.2.68", {"start": v(15.24, 71.4) * mm, "end": v(15.24, 66.33) * mm});
            skCircle(sketch, "E6.0.2.69", {"center": v(66.22, 60.15) * mm, "radius": 5.08 * mm, "construction": true});
            skLineSegment(sketch, "E6.0.2.70", {"start": v(50.48, 62.69) * mm, "end": v(50.48, 57.6) * mm});
            skLineSegment(sketch, "E6.0.2.71", {"start": v(-3.63, 71.4) * mm, "end": v(0.77, 73.95) * mm});
            skLineSegment(sketch, "E6.0.2.72", {"start": v(6.44, 71.4) * mm, "end": v(10.84, 73.95) * mm});
            skLineSegment(sketch, "E6.0.2.73", {"start": v(-8.67, 57.6) * mm, "end": v(-8.67, 62.69) * mm});
            skCircle(sketch, "E6.0.2.74", {"center": v(41.04, 68.87) * mm, "radius": 5.08 * mm, "construction": true});
            skLineSegment(sketch, "E6.0.2.75", {"start": v(46.71, 66.33) * mm, "end": v(46.71, 71.4) * mm});
            skLineSegment(sketch, "E6.0.2.76", {"start": v(16.5, 71.4) * mm, "end": v(20.9, 73.95) * mm});
            skLineSegment(sketch, "E6.0.2.77", {"start": v(5.8, 55.07) * mm, "end": v(1.4, 57.6) * mm});
            skLineSegment(sketch, "E6.0.2.78", {"start": v(30.98, 73.95) * mm, "end": v(35.37, 71.4) * mm});
            skCircle(sketch, "E6.0.2.79", {"center": v(46.08, 60.15) * mm, "radius": 5.08 * mm, "construction": true});
            skLineSegment(sketch, "E6.0.2.80", {"start": v(86.35, 55.07) * mm, "end": v(81.95, 57.6) * mm});
            skLineSegment(sketch, "E6.0.2.81", {"start": v(95.79, 71.4) * mm, "end": v(95.79, 66.33) * mm});
            skLineSegment(sketch, "E6.0.2.82", {"start": v(51.75, 57.6) * mm, "end": v(51.75, 62.69) * mm});
            skLineSegment(sketch, "E6.0.2.83", {"start": v(46.71, 71.4) * mm, "end": v(51.11, 73.95) * mm});
            skCircle(sketch, "E6.0.2.84", {"center": v(30.98, 68.87) * mm, "radius": 5.08 * mm, "construction": true});
            skLineSegment(sketch, "E6.0.2.85", {"start": v(26.58, 71.4) * mm, "end": v(30.98, 73.95) * mm});
            skLineSegment(sketch, "E6.0.2.86", {"start": v(50.48, 57.6) * mm, "end": v(46.08, 55.07) * mm});
            skLineSegment(sketch, "E6.0.2.87", {"start": v(76.28, 55.07) * mm, "end": v(71.89, 57.6) * mm});
            skLineSegment(sketch, "E6.0.2.88", {"start": v(5.17, 71.4) * mm, "end": v(5.17, 66.33) * mm});
            skLineSegment(sketch, "E6.0.2.89", {"start": v(51.11, 63.79) * mm, "end": v(46.71, 66.33) * mm});
            skLineSegment(sketch, "E6.0.2.90", {"start": v(86.35, 65.23) * mm, "end": v(90.75, 62.69) * mm});
            skLineSegment(sketch, "E6.0.2.91", {"start": v(71.89, 57.6) * mm, "end": v(71.89, 62.69) * mm});
            skLineSegment(sketch, "E6.0.2.92", {"start": v(81.32, 63.79) * mm, "end": v(76.92, 66.33) * mm});
            skCircle(sketch, "E6.0.2.93", {"center": v(36, 60.15) * mm, "radius": 5.08 * mm, "construction": true});
            skLineSegment(sketch, "E6.0.2.94", {"start": v(85.72, 71.4) * mm, "end": v(85.72, 66.33) * mm});
            skLineSegment(sketch, "E6.0.2.95", {"start": v(10.84, 63.79) * mm, "end": v(6.44, 66.33) * mm});
            skLineSegment(sketch, "E6.0.2.96", {"start": v(20.27, 62.69) * mm, "end": v(20.27, 57.6) * mm});
            skLineSegment(sketch, "E6.0.2.97", {"start": v(31.61, 57.6) * mm, "end": v(31.61, 62.69) * mm});
            skLineSegment(sketch, "E6.0.2.98", {"start": v(30.34, 62.69) * mm, "end": v(30.34, 57.6) * mm});
            skLineSegment(sketch, "E6.0.2.99", {"start": v(5.17, 66.33) * mm, "end": v(0.77, 63.79) * mm});
            skLineSegment(sketch, "E6.0.2.100", {"start": v(31.61, 62.69) * mm, "end": v(36, 65.23) * mm});
            skLineSegment(sketch, "E6.0.2.101", {"start": v(81.95, 62.69) * mm, "end": v(86.35, 65.23) * mm});
            skLineSegment(sketch, "E6.0.2.102", {"start": v(86.99, 66.33) * mm, "end": v(86.99, 71.4) * mm});
            skLineSegment(sketch, "E6.0.2.103", {"start": v(55.51, 66.33) * mm, "end": v(51.11, 63.79) * mm});
            skLineSegment(sketch, "E6.0.2.104", {"start": v(75.65, 66.33) * mm, "end": v(71.25, 63.79) * mm});
            skLineSegment(sketch, "E6.0.2.105", {"start": v(76.28, 65.23) * mm, "end": v(80.68, 62.69) * mm});
            skLineSegment(sketch, "E6.0.2.106", {"start": v(30.98, 63.79) * mm, "end": v(26.58, 66.33) * mm});
            skLineSegment(sketch, "E6.0.2.107", {"start": v(26.58, 66.33) * mm, "end": v(26.58, 71.4) * mm});
            skLineSegment(sketch, "E6.0.2.108", {"start": v(1.4, 62.69) * mm, "end": v(5.8, 65.23) * mm});
            skLineSegment(sketch, "E6.0.2.109", {"start": v(15.87, 65.23) * mm, "end": v(20.27, 62.69) * mm});
            skLineSegment(sketch, "E6.0.2.110", {"start": v(45.44, 66.33) * mm, "end": v(41.04, 63.79) * mm});
            skLineSegment(sketch, "E6.0.2.111", {"start": v(76.92, 66.33) * mm, "end": v(76.92, 71.4) * mm});
            skLineSegment(sketch, "E6.0.2.112", {"start": v(1.4, 57.6) * mm, "end": v(1.4, 62.69) * mm});
            skLineSegment(sketch, "E6.0.2.113", {"start": v(10.2, 62.69) * mm, "end": v(10.2, 57.6) * mm});
            skLineSegment(sketch, "E6.0.2.114", {"start": v(20.9, 63.79) * mm, "end": v(16.5, 66.33) * mm});
            skLineSegment(sketch, "E6.0.2.115", {"start": v(25.3, 71.4) * mm, "end": v(25.3, 66.33) * mm});
            skCircle(sketch, "E6.0.2.116", {"center": v(15.87, 60.15) * mm, "radius": 5.08 * mm, "construction": true});
            skLineSegment(sketch, "E6.0.2.117", {"start": v(0.13, 62.69) * mm, "end": v(0.13, 57.6) * mm});
            skLineSegment(sketch, "E6.0.2.118", {"start": v(36, 65.23) * mm, "end": v(40.4, 62.69) * mm});
            skLineSegment(sketch, "E6.0.2.119", {"start": v(-8.67, 57.6) * mm, "end": v(1.4, 57.6) * mm, "construction": true});
            skLineSegment(sketch, "E6.0.2.120", {"start": v(41.04, 63.79) * mm, "end": v(36.64, 66.33) * mm});
            skLineSegment(sketch, "E6.0.2.121", {"start": v(11.47, 62.69) * mm, "end": v(15.87, 65.23) * mm});
            skLineSegment(sketch, "E6.0.2.122", {"start": v(41.68, 57.6) * mm, "end": v(41.68, 62.69) * mm});
            skLineSegment(sketch, "E6.0.2.123", {"start": v(6.44, 66.33) * mm, "end": v(6.44, 71.4) * mm});
            skLineSegment(sketch, "E6.0.2.124", {"start": v(51.75, 62.69) * mm, "end": v(56.15, 65.23) * mm});
            skLineSegment(sketch, "E6.0.2.125", {"start": v(40.4, 62.69) * mm, "end": v(40.4, 57.6) * mm});
            skLineSegment(sketch, "E6.0.2.126", {"start": v(25.3, 66.33) * mm, "end": v(20.9, 63.79) * mm});
            skLineSegment(sketch, "E6.0.2.127", {"start": v(70.62, 62.69) * mm, "end": v(70.62, 57.6) * mm});
            skLineSegment(sketch, "E6.0.2.128", {"start": v(35.37, 66.33) * mm, "end": v(30.98, 63.79) * mm});
            skLineSegment(sketch, "E6.0.2.129", {"start": v(46.08, 65.23) * mm, "end": v(50.48, 62.69) * mm});
            skLineSegment(sketch, "E6.0.2.130", {"start": v(21.54, 57.6) * mm, "end": v(21.54, 62.69) * mm});
            skLineSegment(sketch, "E6.0.2.131", {"start": v(35.37, 71.4) * mm, "end": v(35.37, 66.33) * mm});
            skLineSegment(sketch, "E6.0.2.132", {"start": v(85.72, 66.33) * mm, "end": v(81.32, 63.79) * mm});
            skLineSegment(sketch, "E6.0.2.133", {"start": v(71.89, 62.69) * mm, "end": v(76.28, 65.23) * mm});
            skLineSegment(sketch, "E6.0.2.134", {"start": v(21.54, 62.69) * mm, "end": v(25.94, 65.23) * mm});
            skLineSegment(sketch, "E6.0.2.135", {"start": v(91.39, 63.79) * mm, "end": v(86.99, 66.33) * mm});
            skLineSegment(sketch, "E6.0.2.136", {"start": v(75.65, 71.4) * mm, "end": v(75.65, 66.33) * mm});
            skLineSegment(sketch, "E6.0.2.137", {"start": v(15.24, 66.33) * mm, "end": v(10.84, 63.79) * mm});
            skLineSegment(sketch, "E6.0.2.138", {"start": v(36.64, 66.33) * mm, "end": v(36.64, 71.4) * mm});
            skLineSegment(sketch, "E6.0.2.139", {"start": v(5.8, 65.23) * mm, "end": v(10.2, 62.69) * mm});
            skLineSegment(sketch, "E6.0.2.140", {"start": v(25.94, 65.23) * mm, "end": v(30.34, 62.69) * mm});
            skLineSegment(sketch, "E6.0.2.141", {"start": v(11.47, 57.6) * mm, "end": v(11.47, 62.69) * mm});
            skLineSegment(sketch, "E6.0.2.142", {"start": v(0.77, 63.79) * mm, "end": v(1.4, 62.69) * mm, "construction": true});
            skLineSegment(sketch, "E6.0.2.143", {"start": v(-4.27, 65.23) * mm, "end": v(0.13, 62.69) * mm});
            skLineSegment(sketch, "E6.0.2.144", {"start": v(0.77, 63.79) * mm, "end": v(-3.63, 66.33) * mm});
            skLineSegment(sketch, "E6.0.2.145", {"start": v(0.13, 62.69) * mm, "end": v(1.4, 62.69) * mm, "construction": true});
            skLineSegment(sketch, "E6.0.2.146", {"start": v(0.13, 62.69) * mm, "end": v(0.77, 63.79) * mm, "construction": true});
            skLineSegment(sketch, "E6.direction1", {"start": v(-3.63, 31.45) * mm, "end": v(21.77, 31.45) * mm, "construction": true});
            skLineSegment(sketch, "E6.direction2", {"start": v(-3.63, 31.45) * mm, "end": v(-3.63, 48.89) * mm, "construction": true});
            skLineSegment(sketch, "E7", {"start": v(5.8, 37.63) * mm, "end": v(5.17, 36.53) * mm, "construction": true});
            skLineSegment(sketch, "E8", {"start": v(5.8, 37.63) * mm, "end": v(6.44, 36.53) * mm, "construction": true});
            skLineSegment(sketch, "E9", {"start": v(5.17, 36.53) * mm, "end": v(6.44, 36.53) * mm, "construction": true});
            skLineSegment(sketch, "E10.bottom", {"start": v(-21.37, 115.18) * mm, "end": v(108.49, 115.18) * mm});
            skLineSegment(sketch, "E10.top", {"start": v(-21.37, 13.84) * mm, "end": v(108.49, 13.84) * mm});
            skLineSegment(sketch, "E10.left", {"start": v(-21.37, 115.18) * mm, "end": v(-21.37, 13.84) * mm});
            skLineSegment(sketch, "E10.right", {"start": v(108.49, 115.18) * mm, "end": v(108.49, 13.84) * mm});
            skLineSegment(sketch, "E11", {"start": v(0, 0) * mm, "end": v(59.74, 0) * mm, "construction": true});
            skSolve(sketch);
        }
        {
            var Q0;
            Q0=qSketchRegion(id+"F0",true);
            extrude(context, id + "F1", {"entities" : qUnion([Q0]), "depth" : 1.27 * mm});
        }
        {
            var Q0;
            Q0=makeQuery(id+"F1.opExtrude","CAP_FACE",FACE,{"disambiguationData":[OSD([sQuery(id+"F0.wireOp",EDGE,"E0.0"),sQuery(id+"F0.wireOp",EDGE,"E0.1"),sQuery(id+"F0.wireOp",EDGE,"E0.2"),sQuery(id+"F0.wireOp",EDGE,"E0.3"),sQuery(id+"F0.wireOp",EDGE,"E0.4"),sQuery(id+"F0.wireOp",EDGE,"E0.5"),sQuery(id+"F0.wireOp",EDGE,"E1.1.0.0"),sQuery(id+"F0.wireOp",EDGE,"E1.1.0.1"),sQuery(id+"F0.wireOp",EDGE,"E1.1.0.2"),sQuery(id+"F0.wireOp",EDGE,"E1.1.0.3"),sQuery(id+"F0.wireOp",EDGE,"E1.1.0.4"),sQuery(id+"F0.wireOp",EDGE,"E1.1.0.5"),sQuery(id+"F0.wireOp",EDGE,"E1.2.0.0"),sQuery(id+"F0.wireOp",EDGE,"E1.2.0.1"),sQuery(id+"F0.wireOp",EDGE,"E1.2.0.2"),sQuery(id+"F0.wireOp",EDGE,"E1.2.0.3"),sQuery(id+"F0.wireOp",EDGE,"E1.2.0.4"),sQuery(id+"F0.wireOp",EDGE,"E1.2.0.5"),sQuery(id+"F0.wireOp",EDGE,"0f33f7c7-d985-4434-8b08-4c21ebd6a896.0.3.0"),sQuery(id+"F0.wireOp",EDGE,"0f33f7c7-d985-4434-8b08-4c21ebd6a896.3.3.0"),sQuery(id+"F0.wireOp",EDGE,"0f33f7c7-d985-4434-8b08-4c21ebd6a896.6.3.0"),sQuery(id+"F0.wireOp",EDGE,"0f33f7c7-d985-4434-8b08-4c21ebd6a896.9.3.0"),sQuery(id+"F0.wireOp",EDGE,"0f33f7c7-d985-4434-8b08-4c21ebd6a896.12.3.0"),sQuery(id+"F0.wireOp",EDGE,"0f33f7c7-d985-4434-8b08-4c21ebd6a896.15.3.0"),sQuery(id+"F0.wireOp",EDGE,"0f33f7c7-d985-4434-8b08-4c21ebd6a896.0.4.0"),sQuery(id+"F0.wireOp",EDGE,"0f33f7c7-d985-4434-8b08-4c21ebd6a896.3.4.0"),sQuery(id+"F0.wireOp",EDGE,"0f33f7c7-d985-4434-8b08-4c21ebd6a896.6.4.0"),sQuery(id+"F0.wireOp",EDGE,"0f33f7c7-d985-4434-8b08-4c21ebd6a896.9.4.0"),sQuery(id+"F0.wireOp",EDGE,"0f33f7c7-d985-4434-8b08-4c21ebd6a896.12.4.0"),sQuery(id+"F0.wireOp",EDGE,"0f33f7c7-d985-4434-8b08-4c21ebd6a896.15.4.0"),sQuery(id+"F0.wireOp",EDGE,"0f33f7c7-d985-4434-8b08-4c21ebd6a896.0.5.0"),sQuery(id+"F0.wireOp",EDGE,"0f33f7c7-d985-4434-8b08-4c21ebd6a896.3.5.0"),sQuery(id+"F0.wireOp",EDGE,"0f33f7c7-d985-4434-8b08-4c21ebd6a896.6.5.0"),sQuery(id+"F0.wireOp",EDGE,"0f33f7c7-d985-4434-8b08-4c21ebd6a896.9.5.0"),sQuery(id+"F0.wireOp",EDGE,"0f33f7c7-d985-4434-8b08-4c21ebd6a896.12.5.0"),sQuery(id+"F0.wireOp",EDGE,"0f33f7c7-d985-4434-8b08-4c21ebd6a896.15.5.0"),sQuery(id+"F0.wireOp",EDGE,"0f33f7c7-d985-4434-8b08-4c21ebd6a896.0.6.0"),sQuery(id+"F0.wireOp",EDGE,"0f33f7c7-d985-4434-8b08-4c21ebd6a896.3.6.0"),sQuery(id+"F0.wireOp",EDGE,"0f33f7c7-d985-4434-8b08-4c21ebd6a896.6.6.0"),sQuery(id+"F0.wireOp",EDGE,"0f33f7c7-d985-4434-8b08-4c21ebd6a896.9.6.0"),sQuery(id+"F0.wireOp",EDGE,"0f33f7c7-d985-4434-8b08-4c21ebd6a896.12.6.0"),sQuery(id+"F0.wireOp",EDGE,"0f33f7c7-d985-4434-8b08-4c21ebd6a896.15.6.0"),sQuery(id+"F0.wireOp",EDGE,"0f33f7c7-d985-4434-8b08-4c21ebd6a896.0.7.0"),sQuery(id+"F0.wireOp",EDGE,"0f33f7c7-d985-4434-8b08-4c21ebd6a896.3.7.0"),sQuery(id+"F0.wireOp",EDGE,"0f33f7c7-d985-4434-8b08-4c21ebd6a896.6.7.0"),sQuery(id+"F0.wireOp",EDGE,"0f33f7c7-d985-4434-8b08-4c21ebd6a896.9.7.0"),sQuery(id+"F0.wireOp",EDGE,"0f33f7c7-d985-4434-8b08-4c21ebd6a896.12.7.0"),sQuery(id+"F0.wireOp",EDGE,"0f33f7c7-d985-4434-8b08-4c21ebd6a896.15.7.0"),sQuery(id+"F0.wireOp",EDGE,"0f33f7c7-d985-4434-8b08-4c21ebd6a896.0.8.0"),sQuery(id+"F0.wireOp",EDGE,"0f33f7c7-d985-4434-8b08-4c21ebd6a896.3.8.0"),sQuery(id+"F0.wireOp",EDGE,"0f33f7c7-d985-4434-8b08-4c21ebd6a896.6.8.0"),sQuery(id+"F0.wireOp",EDGE,"0f33f7c7-d985-4434-8b08-4c21ebd6a896.9.8.0"),sQuery(id+"F0.wireOp",EDGE,"0f33f7c7-d985-4434-8b08-4c21ebd6a896.12.8.0"),sQuery(id+"F0.wireOp",EDGE,"0f33f7c7-d985-4434-8b08-4c21ebd6a896.15.8.0"),sQuery(id+"F0.wireOp",EDGE,"0f33f7c7-d985-4434-8b08-4c21ebd6a896.0.9.0"),sQuery(id+"F0.wireOp",EDGE,"0f33f7c7-d985-4434-8b08-4c21ebd6a896.3.9.0"),sQuery(id+"F0.wireOp",EDGE,"0f33f7c7-d985-4434-8b08-4c21ebd6a896.6.9.0"),sQuery(id+"F0.wireOp",EDGE,"0f33f7c7-d985-4434-8b08-4c21ebd6a896.9.9.0"),sQuery(id+"F0.wireOp",EDGE,"0f33f7c7-d985-4434-8b08-4c21ebd6a896.12.9.0"),sQuery(id+"F0.wireOp",EDGE,"0f33f7c7-d985-4434-8b08-4c21ebd6a896.15.9.0"),sQuery(id+"F0.wireOp",EDGE,"E2.0.1.1"),sQuery(id+"F0.wireOp",EDGE,"E2.0.1.2"),sQuery(id+"F0.wireOp",EDGE,"E2.0.1.3"),sQuery(id+"F0.wireOp",EDGE,"E2.0.1.5"),sQuery(id+"F0.wireOp",EDGE,"E2.0.1.7"),sQuery(id+"F0.wireOp",EDGE,"E2.0.1.8"),sQuery(id+"F0.wireOp",EDGE,"E2.0.1.9"),sQuery(id+"F0.wireOp",EDGE,"E2.0.1.10"),sQuery(id+"F0.wireOp",EDGE,"E2.0.1.11"),sQuery(id+"F0.wireOp",EDGE,"E2.0.1.12"),sQuery(id+"F0.wireOp",EDGE,"E2.0.1.14"),sQuery(id+"F0.wireOp",EDGE,"E2.0.1.15"),sQuery(id+"F0.wireOp",EDGE,"E2.0.1.16"),sQuery(id+"F0.wireOp",EDGE,"E2.0.1.17"),sQuery(id+"F0.wireOp",EDGE,"E2.0.1.18"),sQuery(id+"F0.wireOp",EDGE,"E2.0.1.19"),sQuery(id+"F0.wireOp",EDGE,"E2.0.1.21"),sQuery(id+"F0.wireOp",EDGE,"E2.0.1.22"),sQuery(id+"F0.wireOp",EDGE,"E2.0.1.23"),sQuery(id+"F0.wireOp",EDGE,"E2.0.1.24"),sQuery(id+"F0.wireOp",EDGE,"E2.0.1.25"),sQuery(id+"F0.wireOp",EDGE,"E2.0.1.26"),sQuery(id+"F0.wireOp",EDGE,"E2.0.1.28"),sQuery(id+"F0.wireOp",EDGE,"E2.0.1.29"),sQuery(id+"F0.wireOp",EDGE,"E2.0.1.30"),sQuery(id+"F0.wireOp",EDGE,"E2.0.1.31"),sQuery(id+"F0.wireOp",EDGE,"E2.0.1.32"),sQuery(id+"F0.wireOp",EDGE,"E2.0.1.33"),sQuery(id+"F0.wireOp",EDGE,"E2.0.1.35"),sQuery(id+"F0.wireOp",EDGE,"E2.0.1.36"),sQuery(id+"F0.wireOp",EDGE,"E2.0.1.37"),sQuery(id+"F0.wireOp",EDGE,"E2.0.1.38"),sQuery(id+"F0.wireOp",EDGE,"E2.0.1.39"),sQuery(id+"F0.wireOp",EDGE,"E2.0.1.40"),sQuery(id+"F0.wireOp",EDGE,"E2.0.1.41"),sQuery(id+"F0.wireOp",EDGE,"E2.0.1.42"),sQuery(id+"F0.wireOp",EDGE,"E2.0.1.44"),sQuery(id+"F0.wireOp",EDGE,"E2.0.1.46"),sQuery(id+"F0.wireOp",EDGE,"E2.0.1.47"),sQuery(id+"F0.wireOp",EDGE,"E2.0.1.48"),sQuery(id+"F0.wireOp",EDGE,"E2.0.1.49"),sQuery(id+"F0.wireOp",EDGE,"E2.0.1.51"),sQuery(id+"F0.wireOp",EDGE,"E2.0.1.52"),sQuery(id+"F0.wireOp",EDGE,"E2.0.1.53"),sQuery(id+"F0.wireOp",EDGE,"E2.0.1.54"),sQuery(id+"F0.wireOp",EDGE,"E2.0.1.55"),sQuery(id+"F0.wireOp",EDGE,"E2.0.1.56"),sQuery(id+"F0.wireOp",EDGE,"E2.0.1.57"),sQuery(id+"F0.wireOp",EDGE,"E2.0.1.58"),sQuery(id+"F0.wireOp",EDGE,"E2.0.1.60"),sQuery(id+"F0.wireOp",EDGE,"E2.0.1.61"),sQuery(id+"F0.wireOp",EDGE,"E2.0.1.62"),sQuery(id+"F0.wireOp",EDGE,"E2.0.1.63"),sQuery(id+"F0.wireOp",EDGE,"E2.0.1.64"),sQuery(id+"F0.wireOp",EDGE,"E2.0.1.65"),sQuery(id+"F0.wireOp",EDGE,"E2.0.1.66"),sQuery(id+"F0.wireOp",EDGE,"E2.0.1.67"),sQuery(id+"F0.wireOp",EDGE,"E2.0.1.68"),sQuery(id+"F0.wireOp",EDGE,"E2.0.1.69"),sQuery(id+"F0.wireOp",EDGE,"E2.0.1.70"),sQuery(id+"F0.wireOp",EDGE,"E6.0.1.2"),sQuery(id+"F0.wireOp",EDGE,"E6.0.1.4"),sQuery(id+"F0.wireOp",EDGE,"E6.0.1.8"),sQuery(id+"F0.wireOp",EDGE,"E6.0.1.10"),sQuery(id+"F0.wireOp",EDGE,"E6.0.1.11"),sQuery(id+"F0.wireOp",EDGE,"E6.0.1.12"),sQuery(id+"F0.wireOp",EDGE,"E6.0.1.13"),sQuery(id+"F0.wireOp",EDGE,"E6.0.1.14"),sQuery(id+"F0.wireOp",EDGE,"E6.0.1.15"),sQuery(id+"F0.wireOp",EDGE,"E6.0.1.16"),sQuery(id+"F0.wireOp",EDGE,"E6.0.1.17"),sQuery(id+"F0.wireOp",EDGE,"E6.0.1.18"),sQuery(id+"F0.wireOp",EDGE,"E6.0.1.20"),sQuery(id+"F0.wireOp",EDGE,"E6.0.1.21"),sQuery(id+"F0.wireOp",EDGE,"E6.0.1.22"),sQuery(id+"F0.wireOp",EDGE,"E6.0.1.23"),sQuery(id+"F0.wireOp",EDGE,"E6.0.1.24"),sQuery(id+"F0.wireOp",EDGE,"E6.0.1.25"),sQuery(id+"F0.wireOp",EDGE,"E6.0.1.26"),sQuery(id+"F0.wireOp",EDGE,"E6.0.1.27"),sQuery(id+"F0.wireOp",EDGE,"E6.0.1.28"),sQuery(id+"F0.wireOp",EDGE,"E6.0.1.29"),sQuery(id+"F0.wireOp",EDGE,"E6.0.1.30"),sQuery(id+"F0.wireOp",EDGE,"E6.0.1.31"),sQuery(id+"F0.wireOp",EDGE,"E6.0.1.33"),sQuery(id+"F0.wireOp",EDGE,"E6.0.1.34"),sQuery(id+"F0.wireOp",EDGE,"E6.0.1.36"),sQuery(id+"F0.wireOp",EDGE,"E6.0.1.37"),sQuery(id+"F0.wireOp",EDGE,"E6.0.1.38"),sQuery(id+"F0.wireOp",EDGE,"E6.0.1.39"),sQuery(id+"F0.wireOp",EDGE,"E6.0.1.41"),sQuery(id+"F0.wireOp",EDGE,"E6.0.1.42"),sQuery(id+"F0.wireOp",EDGE,"E6.0.1.43"),sQuery(id+"F0.wireOp",EDGE,"E6.0.1.44"),sQuery(id+"F0.wireOp",EDGE,"E6.0.1.46"),sQuery(id+"F0.wireOp",EDGE,"E6.0.1.48"),sQuery(id+"F0.wireOp",EDGE,"E6.0.1.49"),sQuery(id+"F0.wireOp",EDGE,"E6.0.1.51"),sQuery(id+"F0.wireOp",EDGE,"E6.0.1.52"),sQuery(id+"F0.wireOp",EDGE,"E6.0.1.53"),sQuery(id+"F0.wireOp",EDGE,"E6.0.1.54"),sQuery(id+"F0.wireOp",EDGE,"E6.0.1.55"),sQuery(id+"F0.wireOp",EDGE,"E6.0.1.57"),sQuery(id+"F0.wireOp",EDGE,"E6.0.1.59"),sQuery(id+"F0.wireOp",EDGE,"E6.0.1.60"),sQuery(id+"F0.wireOp",EDGE,"E6.0.1.62"),sQuery(id+"F0.wireOp",EDGE,"E6.0.1.63"),sQuery(id+"F0.wireOp",EDGE,"E6.0.1.64"),sQuery(id+"F0.wireOp",EDGE,"E6.0.1.65"),sQuery(id+"F0.wireOp",EDGE,"E6.0.1.66"),sQuery(id+"F0.wireOp",EDGE,"E6.0.1.67"),sQuery(id+"F0.wireOp",EDGE,"E6.0.1.68"),sQuery(id+"F0.wireOp",EDGE,"E6.0.1.70"),sQuery(id+"F0.wireOp",EDGE,"E6.0.1.71"),sQuery(id+"F0.wireOp",EDGE,"E6.0.1.72"),sQuery(id+"F0.wireOp",EDGE,"E6.0.1.73"),sQuery(id+"F0.wireOp",EDGE,"E6.0.1.75"),sQuery(id+"F0.wireOp",EDGE,"E6.0.1.76"),sQuery(id+"F0.wireOp",EDGE,"E6.0.1.77"),sQuery(id+"F0.wireOp",EDGE,"E6.0.1.78"),sQuery(id+"F0.wireOp",EDGE,"E6.0.1.80"),sQuery(id+"F0.wireOp",EDGE,"E6.0.1.81"),sQuery(id+"F0.wireOp",EDGE,"E6.0.1.82"),sQuery(id+"F0.wireOp",EDGE,"E6.0.1.83"),sQuery(id+"F0.wireOp",EDGE,"E6.0.1.85"),sQuery(id+"F0.wireOp",EDGE,"E6.0.1.86"),sQuery(id+"F0.wireOp",EDGE,"E6.0.1.87"),sQuery(id+"F0.wireOp",EDGE,"E6.0.1.88"),sQuery(id+"F0.wireOp",EDGE,"E6.0.1.89"),sQuery(id+"F0.wireOp",EDGE,"E6.0.1.90"),sQuery(id+"F0.wireOp",EDGE,"E6.0.1.91"),sQuery(id+"F0.wireOp",EDGE,"E6.0.1.92"),sQuery(id+"F0.wireOp",EDGE,"E6.0.1.94"),sQuery(id+"F0.wireOp",EDGE,"E6.0.1.95"),sQuery(id+"F0.wireOp",EDGE,"E6.0.1.96"),sQuery(id+"F0.wireOp",EDGE,"E6.0.1.97"),sQuery(id+"F0.wireOp",EDGE,"E6.0.1.98"),sQuery(id+"F0.wireOp",EDGE,"E6.0.1.99"),sQuery(id+"F0.wireOp",EDGE,"E6.0.1.100"),sQuery(id+"F0.wireOp",EDGE,"E6.0.1.101"),sQuery(id+"F0.wireOp",EDGE,"E6.0.1.102"),sQuery(id+"F0.wireOp",EDGE,"E6.0.1.103"),sQuery(id+"F0.wireOp",EDGE,"E6.0.1.104"),sQuery(id+"F0.wireOp",EDGE,"E6.0.1.105"),sQuery(id+"F0.wireOp",EDGE,"E6.0.1.106"),sQuery(id+"F0.wireOp",EDGE,"E6.0.1.107"),sQuery(id+"F0.wireOp",EDGE,"E6.0.1.108"),sQuery(id+"F0.wireOp",EDGE,"E6.0.1.109"),sQuery(id+"F0.wireOp",EDGE,"E6.0.1.110"),sQuery(id+"F0.wireOp",EDGE,"E6.0.1.111"),sQuery(id+"F0.wireOp",EDGE,"E6.0.1.112"),sQuery(id+"F0.wireOp",EDGE,"E6.0.1.113"),sQuery(id+"F0.wireOp",EDGE,"E6.0.1.114"),sQuery(id+"F0.wireOp",EDGE,"E6.0.1.115"),sQuery(id+"F0.wireOp",EDGE,"E6.0.1.117"),sQuery(id+"F0.wireOp",EDGE,"E6.0.1.118"),sQuery(id+"F0.wireOp",EDGE,"E6.0.1.120"),sQuery(id+"F0.wireOp",EDGE,"E6.0.1.121"),sQuery(id+"F0.wireOp",EDGE,"E6.0.1.122"),sQuery(id+"F0.wireOp",EDGE,"E6.0.1.123"),sQuery(id+"F0.wireOp",EDGE,"E6.0.1.124"),sQuery(id+"F0.wireOp",EDGE,"E6.0.1.125"),sQuery(id+"F0.wireOp",EDGE,"E6.0.1.126"),sQuery(id+"F0.wireOp",EDGE,"E6.0.1.127"),sQuery(id+"F0.wireOp",EDGE,"E6.0.1.128"),sQuery(id+"F0.wireOp",EDGE,"E6.0.1.129"),sQuery(id+"F0.wireOp",EDGE,"E6.0.1.130"),sQuery(id+"F0.wireOp",EDGE,"E6.0.1.131"),sQuery(id+"F0.wireOp",EDGE,"E6.0.1.132"),sQuery(id+"F0.wireOp",EDGE,"E6.0.1.133"),sQuery(id+"F0.wireOp",EDGE,"E6.0.1.134"),sQuery(id+"F0.wireOp",EDGE,"E6.0.1.135"),sQuery(id+"F0.wireOp",EDGE,"E6.0.1.136"),sQuery(id+"F0.wireOp",EDGE,"E6.0.1.137"),sQuery(id+"F0.wireOp",EDGE,"E6.0.1.138"),sQuery(id+"F0.wireOp",EDGE,"E6.0.1.139"),sQuery(id+"F0.wireOp",EDGE,"E6.0.1.140"),sQuery(id+"F0.wireOp",EDGE,"E6.0.1.141"),sQuery(id+"F0.wireOp",EDGE,"E6.0.1.143"),sQuery(id+"F0.wireOp",EDGE,"E6.0.1.144"),sQuery(id+"F0.wireOp",EDGE,"E6.0.2.2"),sQuery(id+"F0.wireOp",EDGE,"E6.0.2.4"),sQuery(id+"F0.wireOp",EDGE,"E6.0.2.8"),sQuery(id+"F0.wireOp",EDGE,"E6.0.2.10"),sQuery(id+"F0.wireOp",EDGE,"E6.0.2.11"),sQuery(id+"F0.wireOp",EDGE,"E6.0.2.12"),sQuery(id+"F0.wireOp",EDGE,"E6.0.2.13"),sQuery(id+"F0.wireOp",EDGE,"E6.0.2.14"),sQuery(id+"F0.wireOp",EDGE,"E6.0.2.15"),sQuery(id+"F0.wireOp",EDGE,"E6.0.2.16"),sQuery(id+"F0.wireOp",EDGE,"E6.0.2.17"),sQuery(id+"F0.wireOp",EDGE,"E6.0.2.18"),sQuery(id+"F0.wireOp",EDGE,"E6.0.2.20"),sQuery(id+"F0.wireOp",EDGE,"E6.0.2.21"),sQuery(id+"F0.wireOp",EDGE,"E6.0.2.22"),sQuery(id+"F0.wireOp",EDGE,"E6.0.2.23"),sQuery(id+"F0.wireOp",EDGE,"E6.0.2.24"),sQuery(id+"F0.wireOp",EDGE,"E6.0.2.25"),sQuery(id+"F0.wireOp",EDGE,"E6.0.2.26"),sQuery(id+"F0.wireOp",EDGE,"E6.0.2.27"),sQuery(id+"F0.wireOp",EDGE,"E6.0.2.28"),sQuery(id+"F0.wireOp",EDGE,"E6.0.2.29"),sQuery(id+"F0.wireOp",EDGE,"E6.0.2.30"),sQuery(id+"F0.wireOp",EDGE,"E6.0.2.31"),sQuery(id+"F0.wireOp",EDGE,"E6.0.2.33"),sQuery(id+"F0.wireOp",EDGE,"E6.0.2.34"),sQuery(id+"F0.wireOp",EDGE,"E6.0.2.36"),sQuery(id+"F0.wireOp",EDGE,"E6.0.2.37"),sQuery(id+"F0.wireOp",EDGE,"E6.0.2.38"),sQuery(id+"F0.wireOp",EDGE,"E6.0.2.39"),sQuery(id+"F0.wireOp",EDGE,"E6.0.2.41"),sQuery(id+"F0.wireOp",EDGE,"E6.0.2.42"),sQuery(id+"F0.wireOp",EDGE,"E6.0.2.43"),sQuery(id+"F0.wireOp",EDGE,"E6.0.2.44"),sQuery(id+"F0.wireOp",EDGE,"E6.0.2.46"),sQuery(id+"F0.wireOp",EDGE,"E6.0.2.48"),sQuery(id+"F0.wireOp",EDGE,"E6.0.2.49"),sQuery(id+"F0.wireOp",EDGE,"E6.0.2.51"),sQuery(id+"F0.wireOp",EDGE,"E6.0.2.52"),sQuery(id+"F0.wireOp",EDGE,"E6.0.2.53"),sQuery(id+"F0.wireOp",EDGE,"E6.0.2.54"),sQuery(id+"F0.wireOp",EDGE,"E6.0.2.55"),sQuery(id+"F0.wireOp",EDGE,"E6.0.2.57"),sQuery(id+"F0.wireOp",EDGE,"E6.0.2.59"),sQuery(id+"F0.wireOp",EDGE,"E6.0.2.60"),sQuery(id+"F0.wireOp",EDGE,"E6.0.2.62"),sQuery(id+"F0.wireOp",EDGE,"E6.0.2.63"),sQuery(id+"F0.wireOp",EDGE,"E6.0.2.64"),sQuery(id+"F0.wireOp",EDGE,"E6.0.2.65"),sQuery(id+"F0.wireOp",EDGE,"E6.0.2.66"),sQuery(id+"F0.wireOp",EDGE,"E6.0.2.67"),sQuery(id+"F0.wireOp",EDGE,"E6.0.2.68"),sQuery(id+"F0.wireOp",EDGE,"E6.0.2.70"),sQuery(id+"F0.wireOp",EDGE,"E6.0.2.71"),sQuery(id+"F0.wireOp",EDGE,"E6.0.2.72"),sQuery(id+"F0.wireOp",EDGE,"E6.0.2.73"),sQuery(id+"F0.wireOp",EDGE,"E6.0.2.75"),sQuery(id+"F0.wireOp",EDGE,"E6.0.2.76"),sQuery(id+"F0.wireOp",EDGE,"E6.0.2.77"),sQuery(id+"F0.wireOp",EDGE,"E6.0.2.78"),sQuery(id+"F0.wireOp",EDGE,"E6.0.2.80"),sQuery(id+"F0.wireOp",EDGE,"E6.0.2.81"),sQuery(id+"F0.wireOp",EDGE,"E6.0.2.82"),sQuery(id+"F0.wireOp",EDGE,"E6.0.2.83"),sQuery(id+"F0.wireOp",EDGE,"E6.0.2.85"),sQuery(id+"F0.wireOp",EDGE,"E6.0.2.86"),sQuery(id+"F0.wireOp",EDGE,"E6.0.2.87"),sQuery(id+"F0.wireOp",EDGE,"E6.0.2.88"),sQuery(id+"F0.wireOp",EDGE,"E6.0.2.89"),sQuery(id+"F0.wireOp",EDGE,"E6.0.2.90"),sQuery(id+"F0.wireOp",EDGE,"E6.0.2.91"),sQuery(id+"F0.wireOp",EDGE,"E6.0.2.92"),sQuery(id+"F0.wireOp",EDGE,"E6.0.2.94"),sQuery(id+"F0.wireOp",EDGE,"E6.0.2.95"),sQuery(id+"F0.wireOp",EDGE,"E6.0.2.96"),sQuery(id+"F0.wireOp",EDGE,"E6.0.2.97"),sQuery(id+"F0.wireOp",EDGE,"E6.0.2.98"),sQuery(id+"F0.wireOp",EDGE,"E6.0.2.99"),sQuery(id+"F0.wireOp",EDGE,"E6.0.2.100"),sQuery(id+"F0.wireOp",EDGE,"E6.0.2.101"),sQuery(id+"F0.wireOp",EDGE,"E6.0.2.102"),sQuery(id+"F0.wireOp",EDGE,"E6.0.2.103"),sQuery(id+"F0.wireOp",EDGE,"E6.0.2.104"),sQuery(id+"F0.wireOp",EDGE,"E6.0.2.105"),sQuery(id+"F0.wireOp",EDGE,"E6.0.2.106"),sQuery(id+"F0.wireOp",EDGE,"E6.0.2.107"),sQuery(id+"F0.wireOp",EDGE,"E6.0.2.108"),sQuery(id+"F0.wireOp",EDGE,"E6.0.2.109"),sQuery(id+"F0.wireOp",EDGE,"E6.0.2.110"),sQuery(id+"F0.wireOp",EDGE,"E6.0.2.111"),sQuery(id+"F0.wireOp",EDGE,"E6.0.2.112"),sQuery(id+"F0.wireOp",EDGE,"E6.0.2.113"),sQuery(id+"F0.wireOp",EDGE,"E6.0.2.114"),sQuery(id+"F0.wireOp",EDGE,"E6.0.2.115"),sQuery(id+"F0.wireOp",EDGE,"E6.0.2.117"),sQuery(id+"F0.wireOp",EDGE,"E6.0.2.118"),sQuery(id+"F0.wireOp",EDGE,"E6.0.2.120"),sQuery(id+"F0.wireOp",EDGE,"E6.0.2.121"),sQuery(id+"F0.wireOp",EDGE,"E6.0.2.122"),sQuery(id+"F0.wireOp",EDGE,"E6.0.2.123"),sQuery(id+"F0.wireOp",EDGE,"E6.0.2.124"),sQuery(id+"F0.wireOp",EDGE,"E6.0.2.125"),sQuery(id+"F0.wireOp",EDGE,"E6.0.2.126"),sQuery(id+"F0.wireOp",EDGE,"E6.0.2.127"),sQuery(id+"F0.wireOp",EDGE,"E6.0.2.128"),sQuery(id+"F0.wireOp",EDGE,"E6.0.2.129"),sQuery(id+"F0.wireOp",EDGE,"E6.0.2.130"),sQuery(id+"F0.wireOp",EDGE,"E6.0.2.131"),sQuery(id+"F0.wireOp",EDGE,"E6.0.2.132"),sQuery(id+"F0.wireOp",EDGE,"E6.0.2.133"),sQuery(id+"F0.wireOp",EDGE,"E6.0.2.134"),sQuery(id+"F0.wireOp",EDGE,"E6.0.2.135"),sQuery(id+"F0.wireOp",EDGE,"E6.0.2.136"),sQuery(id+"F0.wireOp",EDGE,"E6.0.2.137"),sQuery(id+"F0.wireOp",EDGE,"E6.0.2.138"),sQuery(id+"F0.wireOp",EDGE,"E6.0.2.139"),sQuery(id+"F0.wireOp",EDGE,"E6.0.2.140"),sQuery(id+"F0.wireOp",EDGE,"E6.0.2.141"),sQuery(id+"F0.wireOp",EDGE,"E6.0.2.143"),sQuery(id+"F0.wireOp",EDGE,"E6.0.2.144"),sQuery(id+"F0.wireOp",EDGE,"E6.0.3.2"),sQuery(id+"F0.wireOp",EDGE,"E6.0.3.4"),sQuery(id+"F0.wireOp",EDGE,"E6.0.3.8"),sQuery(id+"F0.wireOp",EDGE,"E6.0.3.10"),sQuery(id+"F0.wireOp",EDGE,"E6.0.3.11"),sQuery(id+"F0.wireOp",EDGE,"E6.0.3.12"),sQuery(id+"F0.wireOp",EDGE,"E6.0.3.13"),sQuery(id+"F0.wireOp",EDGE,"E6.0.3.14"),sQuery(id+"F0.wireOp",EDGE,"E6.0.3.15"),sQuery(id+"F0.wireOp",EDGE,"E6.0.3.16"),sQuery(id+"F0.wireOp",EDGE,"E6.0.3.17"),sQuery(id+"F0.wireOp",EDGE,"E6.0.3.18"),sQuery(id+"F0.wireOp",EDGE,"E6.0.3.20"),sQuery(id+"F0.wireOp",EDGE,"E6.0.3.21"),sQuery(id+"F0.wireOp",EDGE,"E6.0.3.22"),sQuery(id+"F0.wireOp",EDGE,"E6.0.3.23"),sQuery(id+"F0.wireOp",EDGE,"E6.0.3.24"),sQuery(id+"F0.wireOp",EDGE,"E6.0.3.25"),sQuery(id+"F0.wireOp",EDGE,"E6.0.3.26"),sQuery(id+"F0.wireOp",EDGE,"E6.0.3.27"),sQuery(id+"F0.wireOp",EDGE,"E6.0.3.28"),sQuery(id+"F0.wireOp",EDGE,"E6.0.3.29"),sQuery(id+"F0.wireOp",EDGE,"E6.0.3.30"),sQuery(id+"F0.wireOp",EDGE,"E6.0.3.31"),sQuery(id+"F0.wireOp",EDGE,"E6.0.3.33"),sQuery(id+"F0.wireOp",EDGE,"E6.0.3.34"),sQuery(id+"F0.wireOp",EDGE,"E6.0.3.36"),sQuery(id+"F0.wireOp",EDGE,"E6.0.3.37"),sQuery(id+"F0.wireOp",EDGE,"E6.0.3.38"),sQuery(id+"F0.wireOp",EDGE,"E6.0.3.39"),sQuery(id+"F0.wireOp",EDGE,"E6.0.3.41"),sQuery(id+"F0.wireOp",EDGE,"E6.0.3.42"),sQuery(id+"F0.wireOp",EDGE,"E6.0.3.43"),sQuery(id+"F0.wireOp",EDGE,"E6.0.3.44"),sQuery(id+"F0.wireOp",EDGE,"E6.0.3.46"),sQuery(id+"F0.wireOp",EDGE,"E6.0.3.48"),sQuery(id+"F0.wireOp",EDGE,"E6.0.3.49"),sQuery(id+"F0.wireOp",EDGE,"E6.0.3.51"),sQuery(id+"F0.wireOp",EDGE,"E6.0.3.52"),sQuery(id+"F0.wireOp",EDGE,"E6.0.3.53"),sQuery(id+"F0.wireOp",EDGE,"E6.0.3.54"),sQuery(id+"F0.wireOp",EDGE,"E6.0.3.55"),sQuery(id+"F0.wireOp",EDGE,"E6.0.3.57"),sQuery(id+"F0.wireOp",EDGE,"E6.0.3.59"),sQuery(id+"F0.wireOp",EDGE,"E6.0.3.60"),sQuery(id+"F0.wireOp",EDGE,"E6.0.3.62"),sQuery(id+"F0.wireOp",EDGE,"E6.0.3.63"),sQuery(id+"F0.wireOp",EDGE,"E6.0.3.64"),sQuery(id+"F0.wireOp",EDGE,"E6.0.3.65"),sQuery(id+"F0.wireOp",EDGE,"E6.0.3.66"),sQuery(id+"F0.wireOp",EDGE,"E6.0.3.67"),sQuery(id+"F0.wireOp",EDGE,"E6.0.3.68"),sQuery(id+"F0.wireOp",EDGE,"E6.0.3.70"),sQuery(id+"F0.wireOp",EDGE,"E6.0.3.71"),sQuery(id+"F0.wireOp",EDGE,"E6.0.3.72"),sQuery(id+"F0.wireOp",EDGE,"E6.0.3.73"),sQuery(id+"F0.wireOp",EDGE,"E6.0.3.75"),sQuery(id+"F0.wireOp",EDGE,"E6.0.3.76"),sQuery(id+"F0.wireOp",EDGE,"E6.0.3.77"),sQuery(id+"F0.wireOp",EDGE,"E6.0.3.78"),sQuery(id+"F0.wireOp",EDGE,"E6.0.3.80"),sQuery(id+"F0.wireOp",EDGE,"E6.0.3.81"),sQuery(id+"F0.wireOp",EDGE,"E6.0.3.82"),sQuery(id+"F0.wireOp",EDGE,"E6.0.3.83"),sQuery(id+"F0.wireOp",EDGE,"E6.0.3.85"),sQuery(id+"F0.wireOp",EDGE,"E6.0.3.86"),sQuery(id+"F0.wireOp",EDGE,"E6.0.3.87"),sQuery(id+"F0.wireOp",EDGE,"E6.0.3.88"),sQuery(id+"F0.wireOp",EDGE,"E6.0.3.89"),sQuery(id+"F0.wireOp",EDGE,"E6.0.3.90"),sQuery(id+"F0.wireOp",EDGE,"E6.0.3.91"),sQuery(id+"F0.wireOp",EDGE,"E6.0.3.92"),sQuery(id+"F0.wireOp",EDGE,"E6.0.3.94"),sQuery(id+"F0.wireOp",EDGE,"E6.0.3.95"),sQuery(id+"F0.wireOp",EDGE,"E6.0.3.96"),sQuery(id+"F0.wireOp",EDGE,"E6.0.3.97"),sQuery(id+"F0.wireOp",EDGE,"E6.0.3.98"),sQuery(id+"F0.wireOp",EDGE,"E6.0.3.99"),sQuery(id+"F0.wireOp",EDGE,"E6.0.3.100"),sQuery(id+"F0.wireOp",EDGE,"E6.0.3.101"),sQuery(id+"F0.wireOp",EDGE,"E6.0.3.102"),sQuery(id+"F0.wireOp",EDGE,"E6.0.3.103"),sQuery(id+"F0.wireOp",EDGE,"E6.0.3.104"),sQuery(id+"F0.wireOp",EDGE,"E6.0.3.105"),sQuery(id+"F0.wireOp",EDGE,"E6.0.3.106"),sQuery(id+"F0.wireOp",EDGE,"E6.0.3.107"),sQuery(id+"F0.wireOp",EDGE,"E6.0.3.108"),sQuery(id+"F0.wireOp",EDGE,"E6.0.3.109"),sQuery(id+"F0.wireOp",EDGE,"E6.0.3.110"),sQuery(id+"F0.wireOp",EDGE,"E6.0.3.111"),sQuery(id+"F0.wireOp",EDGE,"E6.0.3.112"),sQuery(id+"F0.wireOp",EDGE,"E6.0.3.113"),sQuery(id+"F0.wireOp",EDGE,"E6.0.3.114"),sQuery(id+"F0.wireOp",EDGE,"E6.0.3.115"),sQuery(id+"F0.wireOp",EDGE,"E6.0.3.117"),sQuery(id+"F0.wireOp",EDGE,"E6.0.3.118"),sQuery(id+"F0.wireOp",EDGE,"E6.0.3.120"),sQuery(id+"F0.wireOp",EDGE,"E6.0.3.121"),sQuery(id+"F0.wireOp",EDGE,"E6.0.3.122"),sQuery(id+"F0.wireOp",EDGE,"E6.0.3.123"),sQuery(id+"F0.wireOp",EDGE,"E6.0.3.124"),sQuery(id+"F0.wireOp",EDGE,"E6.0.3.125"),sQuery(id+"F0.wireOp",EDGE,"E6.0.3.126"),sQuery(id+"F0.wireOp",EDGE,"E6.0.3.127"),sQuery(id+"F0.wireOp",EDGE,"E6.0.3.128"),sQuery(id+"F0.wireOp",EDGE,"E6.0.3.129"),sQuery(id+"F0.wireOp",EDGE,"E6.0.3.130"),sQuery(id+"F0.wireOp",EDGE,"E6.0.3.131"),sQuery(id+"F0.wireOp",EDGE,"E6.0.3.132"),sQuery(id+"F0.wireOp",EDGE,"E6.0.3.133"),sQuery(id+"F0.wireOp",EDGE,"E6.0.3.134"),sQuery(id+"F0.wireOp",EDGE,"E6.0.3.135"),sQuery(id+"F0.wireOp",EDGE,"E6.0.3.136"),sQuery(id+"F0.wireOp",EDGE,"E6.0.3.137"),sQuery(id+"F0.wireOp",EDGE,"E6.0.3.138"),sQuery(id+"F0.wireOp",EDGE,"E6.0.3.139"),sQuery(id+"F0.wireOp",EDGE,"E6.0.3.140"),sQuery(id+"F0.wireOp",EDGE,"E6.0.3.141"),sQuery(id+"F0.wireOp",EDGE,"E6.0.3.143"),sQuery(id+"F0.wireOp",EDGE,"E6.0.3.144"),sQuery(id+"F0.wireOp",EDGE,"E6.0.4.2"),sQuery(id+"F0.wireOp",EDGE,"E6.0.4.4"),sQuery(id+"F0.wireOp",EDGE,"E6.0.4.8"),sQuery(id+"F0.wireOp",EDGE,"E6.0.4.10"),sQuery(id+"F0.wireOp",EDGE,"E6.0.4.11"),sQuery(id+"F0.wireOp",EDGE,"E6.0.4.12"),sQuery(id+"F0.wireOp",EDGE,"E6.0.4.13"),sQuery(id+"F0.wireOp",EDGE,"E6.0.4.14"),sQuery(id+"F0.wireOp",EDGE,"E6.0.4.15"),sQuery(id+"F0.wireOp",EDGE,"E6.0.4.16"),sQuery(id+"F0.wireOp",EDGE,"E6.0.4.17"),sQuery(id+"F0.wireOp",EDGE,"E6.0.4.18"),sQuery(id+"F0.wireOp",EDGE,"E6.0.4.20"),sQuery(id+"F0.wireOp",EDGE,"E6.0.4.21"),sQuery(id+"F0.wireOp",EDGE,"E6.0.4.22"),sQuery(id+"F0.wireOp",EDGE,"E6.0.4.23"),sQuery(id+"F0.wireOp",EDGE,"E6.0.4.24"),sQuery(id+"F0.wireOp",EDGE,"E6.0.4.25"),sQuery(id+"F0.wireOp",EDGE,"E6.0.4.26"),sQuery(id+"F0.wireOp",EDGE,"E6.0.4.27"),sQuery(id+"F0.wireOp",EDGE,"E6.0.4.28"),sQuery(id+"F0.wireOp",EDGE,"E6.0.4.29"),sQuery(id+"F0.wireOp",EDGE,"E6.0.4.30"),sQuery(id+"F0.wireOp",EDGE,"E6.0.4.31"),sQuery(id+"F0.wireOp",EDGE,"E6.0.4.33"),sQuery(id+"F0.wireOp",EDGE,"E6.0.4.34"),sQuery(id+"F0.wireOp",EDGE,"E6.0.4.36"),sQuery(id+"F0.wireOp",EDGE,"E6.0.4.37"),sQuery(id+"F0.wireOp",EDGE,"E6.0.4.38"),sQuery(id+"F0.wireOp",EDGE,"E6.0.4.39"),sQuery(id+"F0.wireOp",EDGE,"E6.0.4.41"),sQuery(id+"F0.wireOp",EDGE,"E6.0.4.42"),sQuery(id+"F0.wireOp",EDGE,"E6.0.4.43"),sQuery(id+"F0.wireOp",EDGE,"E6.0.4.44"),sQuery(id+"F0.wireOp",EDGE,"E6.0.4.46"),sQuery(id+"F0.wireOp",EDGE,"E6.0.4.48"),sQuery(id+"F0.wireOp",EDGE,"E6.0.4.49"),sQuery(id+"F0.wireOp",EDGE,"E6.0.4.51"),sQuery(id+"F0.wireOp",EDGE,"E6.0.4.52"),sQuery(id+"F0.wireOp",EDGE,"E6.0.4.53"),sQuery(id+"F0.wireOp",EDGE,"E6.0.4.54"),sQuery(id+"F0.wireOp",EDGE,"E6.0.4.55"),sQuery(id+"F0.wireOp",EDGE,"E6.0.4.57"),sQuery(id+"F0.wireOp",EDGE,"E6.0.4.59"),sQuery(id+"F0.wireOp",EDGE,"E6.0.4.60"),sQuery(id+"F0.wireOp",EDGE,"E6.0.4.62"),sQuery(id+"F0.wireOp",EDGE,"E6.0.4.63"),sQuery(id+"F0.wireOp",EDGE,"E6.0.4.64"),sQuery(id+"F0.wireOp",EDGE,"E6.0.4.65"),sQuery(id+"F0.wireOp",EDGE,"E6.0.4.66"),sQuery(id+"F0.wireOp",EDGE,"E6.0.4.67"),sQuery(id+"F0.wireOp",EDGE,"E6.0.4.68"),sQuery(id+"F0.wireOp",EDGE,"E6.0.4.70"),sQuery(id+"F0.wireOp",EDGE,"E6.0.4.71"),sQuery(id+"F0.wireOp",EDGE,"E6.0.4.72"),sQuery(id+"F0.wireOp",EDGE,"E6.0.4.73"),sQuery(id+"F0.wireOp",EDGE,"E6.0.4.75"),sQuery(id+"F0.wireOp",EDGE,"E6.0.4.76"),sQuery(id+"F0.wireOp",EDGE,"E6.0.4.77"),sQuery(id+"F0.wireOp",EDGE,"E6.0.4.78"),sQuery(id+"F0.wireOp",EDGE,"E6.0.4.80"),sQuery(id+"F0.wireOp",EDGE,"E6.0.4.81"),sQuery(id+"F0.wireOp",EDGE,"E6.0.4.82"),sQuery(id+"F0.wireOp",EDGE,"E6.0.4.83"),sQuery(id+"F0.wireOp",EDGE,"E6.0.4.85"),sQuery(id+"F0.wireOp",EDGE,"E6.0.4.86"),sQuery(id+"F0.wireOp",EDGE,"E6.0.4.87"),sQuery(id+"F0.wireOp",EDGE,"E6.0.4.88"),sQuery(id+"F0.wireOp",EDGE,"E6.0.4.89"),sQuery(id+"F0.wireOp",EDGE,"E6.0.4.90"),sQuery(id+"F0.wireOp",EDGE,"E6.0.4.91"),sQuery(id+"F0.wireOp",EDGE,"E6.0.4.92"),sQuery(id+"F0.wireOp",EDGE,"E6.0.4.94"),sQuery(id+"F0.wireOp",EDGE,"E6.0.4.95"),sQuery(id+"F0.wireOp",EDGE,"E6.0.4.96"),sQuery(id+"F0.wireOp",EDGE,"E6.0.4.97"),sQuery(id+"F0.wireOp",EDGE,"E6.0.4.98"),sQuery(id+"F0.wireOp",EDGE,"E6.0.4.99"),sQuery(id+"F0.wireOp",EDGE,"E6.0.4.100"),sQuery(id+"F0.wireOp",EDGE,"E6.0.4.101"),sQuery(id+"F0.wireOp",EDGE,"E6.0.4.102"),sQuery(id+"F0.wireOp",EDGE,"E6.0.4.103"),sQuery(id+"F0.wireOp",EDGE,"E6.0.4.104"),sQuery(id+"F0.wireOp",EDGE,"E6.0.4.105"),sQuery(id+"F0.wireOp",EDGE,"E6.0.4.106"),sQuery(id+"F0.wireOp",EDGE,"E6.0.4.107"),sQuery(id+"F0.wireOp",EDGE,"E6.0.4.108"),sQuery(id+"F0.wireOp",EDGE,"E6.0.4.109"),sQuery(id+"F0.wireOp",EDGE,"E6.0.4.110"),sQuery(id+"F0.wireOp",EDGE,"E6.0.4.111"),sQuery(id+"F0.wireOp",EDGE,"E6.0.4.112"),sQuery(id+"F0.wireOp",EDGE,"E6.0.4.113"),sQuery(id+"F0.wireOp",EDGE,"E6.0.4.114"),sQuery(id+"F0.wireOp",EDGE,"E6.0.4.115"),sQuery(id+"F0.wireOp",EDGE,"E6.0.4.117"),sQuery(id+"F0.wireOp",EDGE,"E6.0.4.118"),sQuery(id+"F0.wireOp",EDGE,"E6.0.4.120"),sQuery(id+"F0.wireOp",EDGE,"E6.0.4.121"),sQuery(id+"F0.wireOp",EDGE,"E6.0.4.122"),sQuery(id+"F0.wireOp",EDGE,"E6.0.4.123"),sQuery(id+"F0.wireOp",EDGE,"E6.0.4.124"),sQuery(id+"F0.wireOp",EDGE,"E6.0.4.125"),sQuery(id+"F0.wireOp",EDGE,"E6.0.4.126"),sQuery(id+"F0.wireOp",EDGE,"E6.0.4.127"),sQuery(id+"F0.wireOp",EDGE,"E6.0.4.128"),sQuery(id+"F0.wireOp",EDGE,"E6.0.4.129"),sQuery(id+"F0.wireOp",EDGE,"E6.0.4.130"),sQuery(id+"F0.wireOp",EDGE,"E6.0.4.131"),sQuery(id+"F0.wireOp",EDGE,"E6.0.4.132"),sQuery(id+"F0.wireOp",EDGE,"E6.0.4.133"),sQuery(id+"F0.wireOp",EDGE,"E6.0.4.134"),sQuery(id+"F0.wireOp",EDGE,"E6.0.4.135"),sQuery(id+"F0.wireOp",EDGE,"E6.0.4.136"),sQuery(id+"F0.wireOp",EDGE,"E6.0.4.137"),sQuery(id+"F0.wireOp",EDGE,"E6.0.4.138"),sQuery(id+"F0.wireOp",EDGE,"E6.0.4.139"),sQuery(id+"F0.wireOp",EDGE,"E6.0.4.140"),sQuery(id+"F0.wireOp",EDGE,"E6.0.4.141"),sQuery(id+"F0.wireOp",EDGE,"E6.0.4.143"),sQuery(id+"F0.wireOp",EDGE,"E6.0.4.144"),sQuery(id+"F0.wireOp",EDGE,"E10.bottom"),sQuery(id+"F0.wireOp",EDGE,"E10.top"),sQuery(id+"F0.wireOp",EDGE,"E10.left"),sQuery(id+"F0.wireOp",EDGE,"E10.right")])],"isStart":false});
            fillet(context, id + "F2", {"entities" : qUnion([Q0]), "radius" : 0.3 * mm, "tangentPropagation" : true, "allowEdgeOverflow" : false});
        }
        {
            var Q0;
            Q0=makeQuery(id+"F1.opExtrude","SWEPT_BODY",BODY,{"disambiguationData":[OSD([sQuery(id+"F0.wireOp",EDGE,"E0.0"),sQuery(id+"F0.wireOp",EDGE,"E0.1"),sQuery(id+"F0.wireOp",EDGE,"E0.2"),sQuery(id+"F0.wireOp",EDGE,"E0.3"),sQuery(id+"F0.wireOp",EDGE,"E0.4"),sQuery(id+"F0.wireOp",EDGE,"E0.5"),sQuery(id+"F0.wireOp",EDGE,"E1.1.0.0"),sQuery(id+"F0.wireOp",EDGE,"E1.1.0.1"),sQuery(id+"F0.wireOp",EDGE,"E1.1.0.2"),sQuery(id+"F0.wireOp",EDGE,"E1.1.0.3"),sQuery(id+"F0.wireOp",EDGE,"E1.1.0.4"),sQuery(id+"F0.wireOp",EDGE,"E1.1.0.5"),sQuery(id+"F0.wireOp",EDGE,"E1.2.0.0"),sQuery(id+"F0.wireOp",EDGE,"E1.2.0.1"),sQuery(id+"F0.wireOp",EDGE,"E1.2.0.2"),sQuery(id+"F0.wireOp",EDGE,"E1.2.0.3"),sQuery(id+"F0.wireOp",EDGE,"E1.2.0.4"),sQuery(id+"F0.wireOp",EDGE,"E1.2.0.5"),sQuery(id+"F0.wireOp",EDGE,"0f33f7c7-d985-4434-8b08-4c21ebd6a896.0.3.0"),sQuery(id+"F0.wireOp",EDGE,"0f33f7c7-d985-4434-8b08-4c21ebd6a896.3.3.0"),sQuery(id+"F0.wireOp",EDGE,"0f33f7c7-d985-4434-8b08-4c21ebd6a896.6.3.0"),sQuery(id+"F0.wireOp",EDGE,"0f33f7c7-d985-4434-8b08-4c21ebd6a896.9.3.0"),sQuery(id+"F0.wireOp",EDGE,"0f33f7c7-d985-4434-8b08-4c21ebd6a896.12.3.0"),sQuery(id+"F0.wireOp",EDGE,"0f33f7c7-d985-4434-8b08-4c21ebd6a896.15.3.0"),sQuery(id+"F0.wireOp",EDGE,"0f33f7c7-d985-4434-8b08-4c21ebd6a896.0.4.0"),sQuery(id+"F0.wireOp",EDGE,"0f33f7c7-d985-4434-8b08-4c21ebd6a896.3.4.0"),sQuery(id+"F0.wireOp",EDGE,"0f33f7c7-d985-4434-8b08-4c21ebd6a896.6.4.0"),sQuery(id+"F0.wireOp",EDGE,"0f33f7c7-d985-4434-8b08-4c21ebd6a896.9.4.0"),sQuery(id+"F0.wireOp",EDGE,"0f33f7c7-d985-4434-8b08-4c21ebd6a896.12.4.0"),sQuery(id+"F0.wireOp",EDGE,"0f33f7c7-d985-4434-8b08-4c21ebd6a896.15.4.0"),sQuery(id+"F0.wireOp",EDGE,"0f33f7c7-d985-4434-8b08-4c21ebd6a896.0.5.0"),sQuery(id+"F0.wireOp",EDGE,"0f33f7c7-d985-4434-8b08-4c21ebd6a896.3.5.0"),sQuery(id+"F0.wireOp",EDGE,"0f33f7c7-d985-4434-8b08-4c21ebd6a896.6.5.0"),sQuery(id+"F0.wireOp",EDGE,"0f33f7c7-d985-4434-8b08-4c21ebd6a896.9.5.0"),sQuery(id+"F0.wireOp",EDGE,"0f33f7c7-d985-4434-8b08-4c21ebd6a896.12.5.0"),sQuery(id+"F0.wireOp",EDGE,"0f33f7c7-d985-4434-8b08-4c21ebd6a896.15.5.0"),sQuery(id+"F0.wireOp",EDGE,"0f33f7c7-d985-4434-8b08-4c21ebd6a896.0.6.0"),sQuery(id+"F0.wireOp",EDGE,"0f33f7c7-d985-4434-8b08-4c21ebd6a896.3.6.0"),sQuery(id+"F0.wireOp",EDGE,"0f33f7c7-d985-4434-8b08-4c21ebd6a896.6.6.0"),sQuery(id+"F0.wireOp",EDGE,"0f33f7c7-d985-4434-8b08-4c21ebd6a896.9.6.0"),sQuery(id+"F0.wireOp",EDGE,"0f33f7c7-d985-4434-8b08-4c21ebd6a896.12.6.0"),sQuery(id+"F0.wireOp",EDGE,"0f33f7c7-d985-4434-8b08-4c21ebd6a896.15.6.0"),sQuery(id+"F0.wireOp",EDGE,"0f33f7c7-d985-4434-8b08-4c21ebd6a896.0.7.0"),sQuery(id+"F0.wireOp",EDGE,"0f33f7c7-d985-4434-8b08-4c21ebd6a896.3.7.0"),sQuery(id+"F0.wireOp",EDGE,"0f33f7c7-d985-4434-8b08-4c21ebd6a896.6.7.0"),sQuery(id+"F0.wireOp",EDGE,"0f33f7c7-d985-4434-8b08-4c21ebd6a896.9.7.0"),sQuery(id+"F0.wireOp",EDGE,"0f33f7c7-d985-4434-8b08-4c21ebd6a896.12.7.0"),sQuery(id+"F0.wireOp",EDGE,"0f33f7c7-d985-4434-8b08-4c21ebd6a896.15.7.0"),sQuery(id+"F0.wireOp",EDGE,"0f33f7c7-d985-4434-8b08-4c21ebd6a896.0.8.0"),sQuery(id+"F0.wireOp",EDGE,"0f33f7c7-d985-4434-8b08-4c21ebd6a896.3.8.0"),sQuery(id+"F0.wireOp",EDGE,"0f33f7c7-d985-4434-8b08-4c21ebd6a896.6.8.0"),sQuery(id+"F0.wireOp",EDGE,"0f33f7c7-d985-4434-8b08-4c21ebd6a896.9.8.0"),sQuery(id+"F0.wireOp",EDGE,"0f33f7c7-d985-4434-8b08-4c21ebd6a896.12.8.0"),sQuery(id+"F0.wireOp",EDGE,"0f33f7c7-d985-4434-8b08-4c21ebd6a896.15.8.0"),sQuery(id+"F0.wireOp",EDGE,"0f33f7c7-d985-4434-8b08-4c21ebd6a896.0.9.0"),sQuery(id+"F0.wireOp",EDGE,"0f33f7c7-d985-4434-8b08-4c21ebd6a896.3.9.0"),sQuery(id+"F0.wireOp",EDGE,"0f33f7c7-d985-4434-8b08-4c21ebd6a896.6.9.0"),sQuery(id+"F0.wireOp",EDGE,"0f33f7c7-d985-4434-8b08-4c21ebd6a896.9.9.0"),sQuery(id+"F0.wireOp",EDGE,"0f33f7c7-d985-4434-8b08-4c21ebd6a896.12.9.0"),sQuery(id+"F0.wireOp",EDGE,"0f33f7c7-d985-4434-8b08-4c21ebd6a896.15.9.0"),sQuery(id+"F0.wireOp",EDGE,"E2.0.1.1"),sQuery(id+"F0.wireOp",EDGE,"E2.0.1.2"),sQuery(id+"F0.wireOp",EDGE,"E2.0.1.3"),sQuery(id+"F0.wireOp",EDGE,"E2.0.1.5"),sQuery(id+"F0.wireOp",EDGE,"E2.0.1.7"),sQuery(id+"F0.wireOp",EDGE,"E2.0.1.8"),sQuery(id+"F0.wireOp",EDGE,"E2.0.1.9"),sQuery(id+"F0.wireOp",EDGE,"E2.0.1.10"),sQuery(id+"F0.wireOp",EDGE,"E2.0.1.11"),sQuery(id+"F0.wireOp",EDGE,"E2.0.1.12"),sQuery(id+"F0.wireOp",EDGE,"E2.0.1.14"),sQuery(id+"F0.wireOp",EDGE,"E2.0.1.15"),sQuery(id+"F0.wireOp",EDGE,"E2.0.1.16"),sQuery(id+"F0.wireOp",EDGE,"E2.0.1.17"),sQuery(id+"F0.wireOp",EDGE,"E2.0.1.18"),sQuery(id+"F0.wireOp",EDGE,"E2.0.1.19"),sQuery(id+"F0.wireOp",EDGE,"E2.0.1.21"),sQuery(id+"F0.wireOp",EDGE,"E2.0.1.22"),sQuery(id+"F0.wireOp",EDGE,"E2.0.1.23"),sQuery(id+"F0.wireOp",EDGE,"E2.0.1.24"),sQuery(id+"F0.wireOp",EDGE,"E2.0.1.25"),sQuery(id+"F0.wireOp",EDGE,"E2.0.1.26"),sQuery(id+"F0.wireOp",EDGE,"E2.0.1.28"),sQuery(id+"F0.wireOp",EDGE,"E2.0.1.29"),sQuery(id+"F0.wireOp",EDGE,"E2.0.1.30"),sQuery(id+"F0.wireOp",EDGE,"E2.0.1.31"),sQuery(id+"F0.wireOp",EDGE,"E2.0.1.32"),sQuery(id+"F0.wireOp",EDGE,"E2.0.1.33"),sQuery(id+"F0.wireOp",EDGE,"E2.0.1.35"),sQuery(id+"F0.wireOp",EDGE,"E2.0.1.36"),sQuery(id+"F0.wireOp",EDGE,"E2.0.1.37"),sQuery(id+"F0.wireOp",EDGE,"E2.0.1.38"),sQuery(id+"F0.wireOp",EDGE,"E2.0.1.39"),sQuery(id+"F0.wireOp",EDGE,"E2.0.1.40"),sQuery(id+"F0.wireOp",EDGE,"E2.0.1.41"),sQuery(id+"F0.wireOp",EDGE,"E2.0.1.42"),sQuery(id+"F0.wireOp",EDGE,"E2.0.1.44"),sQuery(id+"F0.wireOp",EDGE,"E2.0.1.46"),sQuery(id+"F0.wireOp",EDGE,"E2.0.1.47"),sQuery(id+"F0.wireOp",EDGE,"E2.0.1.48"),sQuery(id+"F0.wireOp",EDGE,"E2.0.1.49"),sQuery(id+"F0.wireOp",EDGE,"E2.0.1.51"),sQuery(id+"F0.wireOp",EDGE,"E2.0.1.52"),sQuery(id+"F0.wireOp",EDGE,"E2.0.1.53"),sQuery(id+"F0.wireOp",EDGE,"E2.0.1.54"),sQuery(id+"F0.wireOp",EDGE,"E2.0.1.55"),sQuery(id+"F0.wireOp",EDGE,"E2.0.1.56"),sQuery(id+"F0.wireOp",EDGE,"E2.0.1.57"),sQuery(id+"F0.wireOp",EDGE,"E2.0.1.58"),sQuery(id+"F0.wireOp",EDGE,"E2.0.1.60"),sQuery(id+"F0.wireOp",EDGE,"E2.0.1.61"),sQuery(id+"F0.wireOp",EDGE,"E2.0.1.62"),sQuery(id+"F0.wireOp",EDGE,"E2.0.1.63"),sQuery(id+"F0.wireOp",EDGE,"E2.0.1.64"),sQuery(id+"F0.wireOp",EDGE,"E2.0.1.65"),sQuery(id+"F0.wireOp",EDGE,"E2.0.1.66"),sQuery(id+"F0.wireOp",EDGE,"E2.0.1.67"),sQuery(id+"F0.wireOp",EDGE,"E2.0.1.68"),sQuery(id+"F0.wireOp",EDGE,"E2.0.1.69"),sQuery(id+"F0.wireOp",EDGE,"E2.0.1.70"),sQuery(id+"F0.wireOp",EDGE,"E6.0.1.2"),sQuery(id+"F0.wireOp",EDGE,"E6.0.1.4"),sQuery(id+"F0.wireOp",EDGE,"E6.0.1.8"),sQuery(id+"F0.wireOp",EDGE,"E6.0.1.10"),sQuery(id+"F0.wireOp",EDGE,"E6.0.1.11"),sQuery(id+"F0.wireOp",EDGE,"E6.0.1.12"),sQuery(id+"F0.wireOp",EDGE,"E6.0.1.13"),sQuery(id+"F0.wireOp",EDGE,"E6.0.1.14"),sQuery(id+"F0.wireOp",EDGE,"E6.0.1.15"),sQuery(id+"F0.wireOp",EDGE,"E6.0.1.16"),sQuery(id+"F0.wireOp",EDGE,"E6.0.1.17"),sQuery(id+"F0.wireOp",EDGE,"E6.0.1.18"),sQuery(id+"F0.wireOp",EDGE,"E6.0.1.20"),sQuery(id+"F0.wireOp",EDGE,"E6.0.1.21"),sQuery(id+"F0.wireOp",EDGE,"E6.0.1.22"),sQuery(id+"F0.wireOp",EDGE,"E6.0.1.23"),sQuery(id+"F0.wireOp",EDGE,"E6.0.1.24"),sQuery(id+"F0.wireOp",EDGE,"E6.0.1.25"),sQuery(id+"F0.wireOp",EDGE,"E6.0.1.26"),sQuery(id+"F0.wireOp",EDGE,"E6.0.1.27"),sQuery(id+"F0.wireOp",EDGE,"E6.0.1.28"),sQuery(id+"F0.wireOp",EDGE,"E6.0.1.29"),sQuery(id+"F0.wireOp",EDGE,"E6.0.1.30"),sQuery(id+"F0.wireOp",EDGE,"E6.0.1.31"),sQuery(id+"F0.wireOp",EDGE,"E6.0.1.33"),sQuery(id+"F0.wireOp",EDGE,"E6.0.1.34"),sQuery(id+"F0.wireOp",EDGE,"E6.0.1.36"),sQuery(id+"F0.wireOp",EDGE,"E6.0.1.37"),sQuery(id+"F0.wireOp",EDGE,"E6.0.1.38"),sQuery(id+"F0.wireOp",EDGE,"E6.0.1.39"),sQuery(id+"F0.wireOp",EDGE,"E6.0.1.41"),sQuery(id+"F0.wireOp",EDGE,"E6.0.1.42"),sQuery(id+"F0.wireOp",EDGE,"E6.0.1.43"),sQuery(id+"F0.wireOp",EDGE,"E6.0.1.44"),sQuery(id+"F0.wireOp",EDGE,"E6.0.1.46"),sQuery(id+"F0.wireOp",EDGE,"E6.0.1.48"),sQuery(id+"F0.wireOp",EDGE,"E6.0.1.49"),sQuery(id+"F0.wireOp",EDGE,"E6.0.1.51"),sQuery(id+"F0.wireOp",EDGE,"E6.0.1.52"),sQuery(id+"F0.wireOp",EDGE,"E6.0.1.53"),sQuery(id+"F0.wireOp",EDGE,"E6.0.1.54"),sQuery(id+"F0.wireOp",EDGE,"E6.0.1.55"),sQuery(id+"F0.wireOp",EDGE,"E6.0.1.57"),sQuery(id+"F0.wireOp",EDGE,"E6.0.1.59"),sQuery(id+"F0.wireOp",EDGE,"E6.0.1.60"),sQuery(id+"F0.wireOp",EDGE,"E6.0.1.62"),sQuery(id+"F0.wireOp",EDGE,"E6.0.1.63"),sQuery(id+"F0.wireOp",EDGE,"E6.0.1.64"),sQuery(id+"F0.wireOp",EDGE,"E6.0.1.65"),sQuery(id+"F0.wireOp",EDGE,"E6.0.1.66"),sQuery(id+"F0.wireOp",EDGE,"E6.0.1.67"),sQuery(id+"F0.wireOp",EDGE,"E6.0.1.68"),sQuery(id+"F0.wireOp",EDGE,"E6.0.1.70"),sQuery(id+"F0.wireOp",EDGE,"E6.0.1.71"),sQuery(id+"F0.wireOp",EDGE,"E6.0.1.72"),sQuery(id+"F0.wireOp",EDGE,"E6.0.1.73"),sQuery(id+"F0.wireOp",EDGE,"E6.0.1.75"),sQuery(id+"F0.wireOp",EDGE,"E6.0.1.76"),sQuery(id+"F0.wireOp",EDGE,"E6.0.1.77"),sQuery(id+"F0.wireOp",EDGE,"E6.0.1.78"),sQuery(id+"F0.wireOp",EDGE,"E6.0.1.80"),sQuery(id+"F0.wireOp",EDGE,"E6.0.1.81"),sQuery(id+"F0.wireOp",EDGE,"E6.0.1.82"),sQuery(id+"F0.wireOp",EDGE,"E6.0.1.83"),sQuery(id+"F0.wireOp",EDGE,"E6.0.1.85"),sQuery(id+"F0.wireOp",EDGE,"E6.0.1.86"),sQuery(id+"F0.wireOp",EDGE,"E6.0.1.87"),sQuery(id+"F0.wireOp",EDGE,"E6.0.1.88"),sQuery(id+"F0.wireOp",EDGE,"E6.0.1.89"),sQuery(id+"F0.wireOp",EDGE,"E6.0.1.90"),sQuery(id+"F0.wireOp",EDGE,"E6.0.1.91"),sQuery(id+"F0.wireOp",EDGE,"E6.0.1.92"),sQuery(id+"F0.wireOp",EDGE,"E6.0.1.94"),sQuery(id+"F0.wireOp",EDGE,"E6.0.1.95"),sQuery(id+"F0.wireOp",EDGE,"E6.0.1.96"),sQuery(id+"F0.wireOp",EDGE,"E6.0.1.97"),sQuery(id+"F0.wireOp",EDGE,"E6.0.1.98"),sQuery(id+"F0.wireOp",EDGE,"E6.0.1.99"),sQuery(id+"F0.wireOp",EDGE,"E6.0.1.100"),sQuery(id+"F0.wireOp",EDGE,"E6.0.1.101"),sQuery(id+"F0.wireOp",EDGE,"E6.0.1.102"),sQuery(id+"F0.wireOp",EDGE,"E6.0.1.103"),sQuery(id+"F0.wireOp",EDGE,"E6.0.1.104"),sQuery(id+"F0.wireOp",EDGE,"E6.0.1.105"),sQuery(id+"F0.wireOp",EDGE,"E6.0.1.106"),sQuery(id+"F0.wireOp",EDGE,"E6.0.1.107"),sQuery(id+"F0.wireOp",EDGE,"E6.0.1.108"),sQuery(id+"F0.wireOp",EDGE,"E6.0.1.109"),sQuery(id+"F0.wireOp",EDGE,"E6.0.1.110"),sQuery(id+"F0.wireOp",EDGE,"E6.0.1.111"),sQuery(id+"F0.wireOp",EDGE,"E6.0.1.112"),sQuery(id+"F0.wireOp",EDGE,"E6.0.1.113"),sQuery(id+"F0.wireOp",EDGE,"E6.0.1.114"),sQuery(id+"F0.wireOp",EDGE,"E6.0.1.115"),sQuery(id+"F0.wireOp",EDGE,"E6.0.1.117"),sQuery(id+"F0.wireOp",EDGE,"E6.0.1.118"),sQuery(id+"F0.wireOp",EDGE,"E6.0.1.120"),sQuery(id+"F0.wireOp",EDGE,"E6.0.1.121"),sQuery(id+"F0.wireOp",EDGE,"E6.0.1.122"),sQuery(id+"F0.wireOp",EDGE,"E6.0.1.123"),sQuery(id+"F0.wireOp",EDGE,"E6.0.1.124"),sQuery(id+"F0.wireOp",EDGE,"E6.0.1.125"),sQuery(id+"F0.wireOp",EDGE,"E6.0.1.126"),sQuery(id+"F0.wireOp",EDGE,"E6.0.1.127"),sQuery(id+"F0.wireOp",EDGE,"E6.0.1.128"),sQuery(id+"F0.wireOp",EDGE,"E6.0.1.129"),sQuery(id+"F0.wireOp",EDGE,"E6.0.1.130"),sQuery(id+"F0.wireOp",EDGE,"E6.0.1.131"),sQuery(id+"F0.wireOp",EDGE,"E6.0.1.132"),sQuery(id+"F0.wireOp",EDGE,"E6.0.1.133"),sQuery(id+"F0.wireOp",EDGE,"E6.0.1.134"),sQuery(id+"F0.wireOp",EDGE,"E6.0.1.135"),sQuery(id+"F0.wireOp",EDGE,"E6.0.1.136"),sQuery(id+"F0.wireOp",EDGE,"E6.0.1.137"),sQuery(id+"F0.wireOp",EDGE,"E6.0.1.138"),sQuery(id+"F0.wireOp",EDGE,"E6.0.1.139"),sQuery(id+"F0.wireOp",EDGE,"E6.0.1.140"),sQuery(id+"F0.wireOp",EDGE,"E6.0.1.141"),sQuery(id+"F0.wireOp",EDGE,"E6.0.1.143"),sQuery(id+"F0.wireOp",EDGE,"E6.0.1.144"),sQuery(id+"F0.wireOp",EDGE,"E6.0.2.2"),sQuery(id+"F0.wireOp",EDGE,"E6.0.2.4"),sQuery(id+"F0.wireOp",EDGE,"E6.0.2.8"),sQuery(id+"F0.wireOp",EDGE,"E6.0.2.10"),sQuery(id+"F0.wireOp",EDGE,"E6.0.2.11"),sQuery(id+"F0.wireOp",EDGE,"E6.0.2.12"),sQuery(id+"F0.wireOp",EDGE,"E6.0.2.13"),sQuery(id+"F0.wireOp",EDGE,"E6.0.2.14"),sQuery(id+"F0.wireOp",EDGE,"E6.0.2.15"),sQuery(id+"F0.wireOp",EDGE,"E6.0.2.16"),sQuery(id+"F0.wireOp",EDGE,"E6.0.2.17"),sQuery(id+"F0.wireOp",EDGE,"E6.0.2.18"),sQuery(id+"F0.wireOp",EDGE,"E6.0.2.20"),sQuery(id+"F0.wireOp",EDGE,"E6.0.2.21"),sQuery(id+"F0.wireOp",EDGE,"E6.0.2.22"),sQuery(id+"F0.wireOp",EDGE,"E6.0.2.23"),sQuery(id+"F0.wireOp",EDGE,"E6.0.2.24"),sQuery(id+"F0.wireOp",EDGE,"E6.0.2.25"),sQuery(id+"F0.wireOp",EDGE,"E6.0.2.26"),sQuery(id+"F0.wireOp",EDGE,"E6.0.2.27"),sQuery(id+"F0.wireOp",EDGE,"E6.0.2.28"),sQuery(id+"F0.wireOp",EDGE,"E6.0.2.29"),sQuery(id+"F0.wireOp",EDGE,"E6.0.2.30"),sQuery(id+"F0.wireOp",EDGE,"E6.0.2.31"),sQuery(id+"F0.wireOp",EDGE,"E6.0.2.33"),sQuery(id+"F0.wireOp",EDGE,"E6.0.2.34"),sQuery(id+"F0.wireOp",EDGE,"E6.0.2.36"),sQuery(id+"F0.wireOp",EDGE,"E6.0.2.37"),sQuery(id+"F0.wireOp",EDGE,"E6.0.2.38"),sQuery(id+"F0.wireOp",EDGE,"E6.0.2.39"),sQuery(id+"F0.wireOp",EDGE,"E6.0.2.41"),sQuery(id+"F0.wireOp",EDGE,"E6.0.2.42"),sQuery(id+"F0.wireOp",EDGE,"E6.0.2.43"),sQuery(id+"F0.wireOp",EDGE,"E6.0.2.44"),sQuery(id+"F0.wireOp",EDGE,"E6.0.2.46"),sQuery(id+"F0.wireOp",EDGE,"E6.0.2.48"),sQuery(id+"F0.wireOp",EDGE,"E6.0.2.49"),sQuery(id+"F0.wireOp",EDGE,"E6.0.2.51"),sQuery(id+"F0.wireOp",EDGE,"E6.0.2.52"),sQuery(id+"F0.wireOp",EDGE,"E6.0.2.53"),sQuery(id+"F0.wireOp",EDGE,"E6.0.2.54"),sQuery(id+"F0.wireOp",EDGE,"E6.0.2.55"),sQuery(id+"F0.wireOp",EDGE,"E6.0.2.57"),sQuery(id+"F0.wireOp",EDGE,"E6.0.2.59"),sQuery(id+"F0.wireOp",EDGE,"E6.0.2.60"),sQuery(id+"F0.wireOp",EDGE,"E6.0.2.62"),sQuery(id+"F0.wireOp",EDGE,"E6.0.2.63"),sQuery(id+"F0.wireOp",EDGE,"E6.0.2.64"),sQuery(id+"F0.wireOp",EDGE,"E6.0.2.65"),sQuery(id+"F0.wireOp",EDGE,"E6.0.2.66"),sQuery(id+"F0.wireOp",EDGE,"E6.0.2.67"),sQuery(id+"F0.wireOp",EDGE,"E6.0.2.68"),sQuery(id+"F0.wireOp",EDGE,"E6.0.2.70"),sQuery(id+"F0.wireOp",EDGE,"E6.0.2.71"),sQuery(id+"F0.wireOp",EDGE,"E6.0.2.72"),sQuery(id+"F0.wireOp",EDGE,"E6.0.2.73"),sQuery(id+"F0.wireOp",EDGE,"E6.0.2.75"),sQuery(id+"F0.wireOp",EDGE,"E6.0.2.76"),sQuery(id+"F0.wireOp",EDGE,"E6.0.2.77"),sQuery(id+"F0.wireOp",EDGE,"E6.0.2.78"),sQuery(id+"F0.wireOp",EDGE,"E6.0.2.80"),sQuery(id+"F0.wireOp",EDGE,"E6.0.2.81"),sQuery(id+"F0.wireOp",EDGE,"E6.0.2.82"),sQuery(id+"F0.wireOp",EDGE,"E6.0.2.83"),sQuery(id+"F0.wireOp",EDGE,"E6.0.2.85"),sQuery(id+"F0.wireOp",EDGE,"E6.0.2.86"),sQuery(id+"F0.wireOp",EDGE,"E6.0.2.87"),sQuery(id+"F0.wireOp",EDGE,"E6.0.2.88"),sQuery(id+"F0.wireOp",EDGE,"E6.0.2.89"),sQuery(id+"F0.wireOp",EDGE,"E6.0.2.90"),sQuery(id+"F0.wireOp",EDGE,"E6.0.2.91"),sQuery(id+"F0.wireOp",EDGE,"E6.0.2.92"),sQuery(id+"F0.wireOp",EDGE,"E6.0.2.94"),sQuery(id+"F0.wireOp",EDGE,"E6.0.2.95"),sQuery(id+"F0.wireOp",EDGE,"E6.0.2.96"),sQuery(id+"F0.wireOp",EDGE,"E6.0.2.97"),sQuery(id+"F0.wireOp",EDGE,"E6.0.2.98"),sQuery(id+"F0.wireOp",EDGE,"E6.0.2.99"),sQuery(id+"F0.wireOp",EDGE,"E6.0.2.100"),sQuery(id+"F0.wireOp",EDGE,"E6.0.2.101"),sQuery(id+"F0.wireOp",EDGE,"E6.0.2.102"),sQuery(id+"F0.wireOp",EDGE,"E6.0.2.103"),sQuery(id+"F0.wireOp",EDGE,"E6.0.2.104"),sQuery(id+"F0.wireOp",EDGE,"E6.0.2.105"),sQuery(id+"F0.wireOp",EDGE,"E6.0.2.106"),sQuery(id+"F0.wireOp",EDGE,"E6.0.2.107"),sQuery(id+"F0.wireOp",EDGE,"E6.0.2.108"),sQuery(id+"F0.wireOp",EDGE,"E6.0.2.109"),sQuery(id+"F0.wireOp",EDGE,"E6.0.2.110"),sQuery(id+"F0.wireOp",EDGE,"E6.0.2.111"),sQuery(id+"F0.wireOp",EDGE,"E6.0.2.112"),sQuery(id+"F0.wireOp",EDGE,"E6.0.2.113"),sQuery(id+"F0.wireOp",EDGE,"E6.0.2.114"),sQuery(id+"F0.wireOp",EDGE,"E6.0.2.115"),sQuery(id+"F0.wireOp",EDGE,"E6.0.2.117"),sQuery(id+"F0.wireOp",EDGE,"E6.0.2.118"),sQuery(id+"F0.wireOp",EDGE,"E6.0.2.120"),sQuery(id+"F0.wireOp",EDGE,"E6.0.2.121"),sQuery(id+"F0.wireOp",EDGE,"E6.0.2.122"),sQuery(id+"F0.wireOp",EDGE,"E6.0.2.123"),sQuery(id+"F0.wireOp",EDGE,"E6.0.2.124"),sQuery(id+"F0.wireOp",EDGE,"E6.0.2.125"),sQuery(id+"F0.wireOp",EDGE,"E6.0.2.126"),sQuery(id+"F0.wireOp",EDGE,"E6.0.2.127"),sQuery(id+"F0.wireOp",EDGE,"E6.0.2.128"),sQuery(id+"F0.wireOp",EDGE,"E6.0.2.129"),sQuery(id+"F0.wireOp",EDGE,"E6.0.2.130"),sQuery(id+"F0.wireOp",EDGE,"E6.0.2.131"),sQuery(id+"F0.wireOp",EDGE,"E6.0.2.132"),sQuery(id+"F0.wireOp",EDGE,"E6.0.2.133"),sQuery(id+"F0.wireOp",EDGE,"E6.0.2.134"),sQuery(id+"F0.wireOp",EDGE,"E6.0.2.135"),sQuery(id+"F0.wireOp",EDGE,"E6.0.2.136"),sQuery(id+"F0.wireOp",EDGE,"E6.0.2.137"),sQuery(id+"F0.wireOp",EDGE,"E6.0.2.138"),sQuery(id+"F0.wireOp",EDGE,"E6.0.2.139"),sQuery(id+"F0.wireOp",EDGE,"E6.0.2.140"),sQuery(id+"F0.wireOp",EDGE,"E6.0.2.141"),sQuery(id+"F0.wireOp",EDGE,"E6.0.2.143"),sQuery(id+"F0.wireOp",EDGE,"E6.0.2.144"),sQuery(id+"F0.wireOp",EDGE,"E6.0.3.2"),sQuery(id+"F0.wireOp",EDGE,"E6.0.3.4"),sQuery(id+"F0.wireOp",EDGE,"E6.0.3.8"),sQuery(id+"F0.wireOp",EDGE,"E6.0.3.10"),sQuery(id+"F0.wireOp",EDGE,"E6.0.3.11"),sQuery(id+"F0.wireOp",EDGE,"E6.0.3.12"),sQuery(id+"F0.wireOp",EDGE,"E6.0.3.13"),sQuery(id+"F0.wireOp",EDGE,"E6.0.3.14"),sQuery(id+"F0.wireOp",EDGE,"E6.0.3.15"),sQuery(id+"F0.wireOp",EDGE,"E6.0.3.16"),sQuery(id+"F0.wireOp",EDGE,"E6.0.3.17"),sQuery(id+"F0.wireOp",EDGE,"E6.0.3.18"),sQuery(id+"F0.wireOp",EDGE,"E6.0.3.20"),sQuery(id+"F0.wireOp",EDGE,"E6.0.3.21"),sQuery(id+"F0.wireOp",EDGE,"E6.0.3.22"),sQuery(id+"F0.wireOp",EDGE,"E6.0.3.23"),sQuery(id+"F0.wireOp",EDGE,"E6.0.3.24"),sQuery(id+"F0.wireOp",EDGE,"E6.0.3.25"),sQuery(id+"F0.wireOp",EDGE,"E6.0.3.26"),sQuery(id+"F0.wireOp",EDGE,"E6.0.3.27"),sQuery(id+"F0.wireOp",EDGE,"E6.0.3.28"),sQuery(id+"F0.wireOp",EDGE,"E6.0.3.29"),sQuery(id+"F0.wireOp",EDGE,"E6.0.3.30"),sQuery(id+"F0.wireOp",EDGE,"E6.0.3.31"),sQuery(id+"F0.wireOp",EDGE,"E6.0.3.33"),sQuery(id+"F0.wireOp",EDGE,"E6.0.3.34"),sQuery(id+"F0.wireOp",EDGE,"E6.0.3.36"),sQuery(id+"F0.wireOp",EDGE,"E6.0.3.37"),sQuery(id+"F0.wireOp",EDGE,"E6.0.3.38"),sQuery(id+"F0.wireOp",EDGE,"E6.0.3.39"),sQuery(id+"F0.wireOp",EDGE,"E6.0.3.41"),sQuery(id+"F0.wireOp",EDGE,"E6.0.3.42"),sQuery(id+"F0.wireOp",EDGE,"E6.0.3.43"),sQuery(id+"F0.wireOp",EDGE,"E6.0.3.44"),sQuery(id+"F0.wireOp",EDGE,"E6.0.3.46"),sQuery(id+"F0.wireOp",EDGE,"E6.0.3.48"),sQuery(id+"F0.wireOp",EDGE,"E6.0.3.49"),sQuery(id+"F0.wireOp",EDGE,"E6.0.3.51"),sQuery(id+"F0.wireOp",EDGE,"E6.0.3.52"),sQuery(id+"F0.wireOp",EDGE,"E6.0.3.53"),sQuery(id+"F0.wireOp",EDGE,"E6.0.3.54"),sQuery(id+"F0.wireOp",EDGE,"E6.0.3.55"),sQuery(id+"F0.wireOp",EDGE,"E6.0.3.57"),sQuery(id+"F0.wireOp",EDGE,"E6.0.3.59"),sQuery(id+"F0.wireOp",EDGE,"E6.0.3.60"),sQuery(id+"F0.wireOp",EDGE,"E6.0.3.62"),sQuery(id+"F0.wireOp",EDGE,"E6.0.3.63"),sQuery(id+"F0.wireOp",EDGE,"E6.0.3.64"),sQuery(id+"F0.wireOp",EDGE,"E6.0.3.65"),sQuery(id+"F0.wireOp",EDGE,"E6.0.3.66"),sQuery(id+"F0.wireOp",EDGE,"E6.0.3.67"),sQuery(id+"F0.wireOp",EDGE,"E6.0.3.68"),sQuery(id+"F0.wireOp",EDGE,"E6.0.3.70"),sQuery(id+"F0.wireOp",EDGE,"E6.0.3.71"),sQuery(id+"F0.wireOp",EDGE,"E6.0.3.72"),sQuery(id+"F0.wireOp",EDGE,"E6.0.3.73"),sQuery(id+"F0.wireOp",EDGE,"E6.0.3.75"),sQuery(id+"F0.wireOp",EDGE,"E6.0.3.76"),sQuery(id+"F0.wireOp",EDGE,"E6.0.3.77"),sQuery(id+"F0.wireOp",EDGE,"E6.0.3.78"),sQuery(id+"F0.wireOp",EDGE,"E6.0.3.80"),sQuery(id+"F0.wireOp",EDGE,"E6.0.3.81"),sQuery(id+"F0.wireOp",EDGE,"E6.0.3.82"),sQuery(id+"F0.wireOp",EDGE,"E6.0.3.83"),sQuery(id+"F0.wireOp",EDGE,"E6.0.3.85"),sQuery(id+"F0.wireOp",EDGE,"E6.0.3.86"),sQuery(id+"F0.wireOp",EDGE,"E6.0.3.87"),sQuery(id+"F0.wireOp",EDGE,"E6.0.3.88"),sQuery(id+"F0.wireOp",EDGE,"E6.0.3.89"),sQuery(id+"F0.wireOp",EDGE,"E6.0.3.90"),sQuery(id+"F0.wireOp",EDGE,"E6.0.3.91"),sQuery(id+"F0.wireOp",EDGE,"E6.0.3.92"),sQuery(id+"F0.wireOp",EDGE,"E6.0.3.94"),sQuery(id+"F0.wireOp",EDGE,"E6.0.3.95"),sQuery(id+"F0.wireOp",EDGE,"E6.0.3.96"),sQuery(id+"F0.wireOp",EDGE,"E6.0.3.97"),sQuery(id+"F0.wireOp",EDGE,"E6.0.3.98"),sQuery(id+"F0.wireOp",EDGE,"E6.0.3.99"),sQuery(id+"F0.wireOp",EDGE,"E6.0.3.100"),sQuery(id+"F0.wireOp",EDGE,"E6.0.3.101"),sQuery(id+"F0.wireOp",EDGE,"E6.0.3.102"),sQuery(id+"F0.wireOp",EDGE,"E6.0.3.103"),sQuery(id+"F0.wireOp",EDGE,"E6.0.3.104"),sQuery(id+"F0.wireOp",EDGE,"E6.0.3.105"),sQuery(id+"F0.wireOp",EDGE,"E6.0.3.106"),sQuery(id+"F0.wireOp",EDGE,"E6.0.3.107"),sQuery(id+"F0.wireOp",EDGE,"E6.0.3.108"),sQuery(id+"F0.wireOp",EDGE,"E6.0.3.109"),sQuery(id+"F0.wireOp",EDGE,"E6.0.3.110"),sQuery(id+"F0.wireOp",EDGE,"E6.0.3.111"),sQuery(id+"F0.wireOp",EDGE,"E6.0.3.112"),sQuery(id+"F0.wireOp",EDGE,"E6.0.3.113"),sQuery(id+"F0.wireOp",EDGE,"E6.0.3.114"),sQuery(id+"F0.wireOp",EDGE,"E6.0.3.115"),sQuery(id+"F0.wireOp",EDGE,"E6.0.3.117"),sQuery(id+"F0.wireOp",EDGE,"E6.0.3.118"),sQuery(id+"F0.wireOp",EDGE,"E6.0.3.120"),sQuery(id+"F0.wireOp",EDGE,"E6.0.3.121"),sQuery(id+"F0.wireOp",EDGE,"E6.0.3.122"),sQuery(id+"F0.wireOp",EDGE,"E6.0.3.123"),sQuery(id+"F0.wireOp",EDGE,"E6.0.3.124"),sQuery(id+"F0.wireOp",EDGE,"E6.0.3.125"),sQuery(id+"F0.wireOp",EDGE,"E6.0.3.126"),sQuery(id+"F0.wireOp",EDGE,"E6.0.3.127"),sQuery(id+"F0.wireOp",EDGE,"E6.0.3.128"),sQuery(id+"F0.wireOp",EDGE,"E6.0.3.129"),sQuery(id+"F0.wireOp",EDGE,"E6.0.3.130"),sQuery(id+"F0.wireOp",EDGE,"E6.0.3.131"),sQuery(id+"F0.wireOp",EDGE,"E6.0.3.132"),sQuery(id+"F0.wireOp",EDGE,"E6.0.3.133"),sQuery(id+"F0.wireOp",EDGE,"E6.0.3.134"),sQuery(id+"F0.wireOp",EDGE,"E6.0.3.135"),sQuery(id+"F0.wireOp",EDGE,"E6.0.3.136"),sQuery(id+"F0.wireOp",EDGE,"E6.0.3.137"),sQuery(id+"F0.wireOp",EDGE,"E6.0.3.138"),sQuery(id+"F0.wireOp",EDGE,"E6.0.3.139"),sQuery(id+"F0.wireOp",EDGE,"E6.0.3.140"),sQuery(id+"F0.wireOp",EDGE,"E6.0.3.141"),sQuery(id+"F0.wireOp",EDGE,"E6.0.3.143"),sQuery(id+"F0.wireOp",EDGE,"E6.0.3.144"),sQuery(id+"F0.wireOp",EDGE,"E6.0.4.2"),sQuery(id+"F0.wireOp",EDGE,"E6.0.4.4"),sQuery(id+"F0.wireOp",EDGE,"E6.0.4.8"),sQuery(id+"F0.wireOp",EDGE,"E6.0.4.10"),sQuery(id+"F0.wireOp",EDGE,"E6.0.4.11"),sQuery(id+"F0.wireOp",EDGE,"E6.0.4.12"),sQuery(id+"F0.wireOp",EDGE,"E6.0.4.13"),sQuery(id+"F0.wireOp",EDGE,"E6.0.4.14"),sQuery(id+"F0.wireOp",EDGE,"E6.0.4.15"),sQuery(id+"F0.wireOp",EDGE,"E6.0.4.16"),sQuery(id+"F0.wireOp",EDGE,"E6.0.4.17"),sQuery(id+"F0.wireOp",EDGE,"E6.0.4.18"),sQuery(id+"F0.wireOp",EDGE,"E6.0.4.20"),sQuery(id+"F0.wireOp",EDGE,"E6.0.4.21"),sQuery(id+"F0.wireOp",EDGE,"E6.0.4.22"),sQuery(id+"F0.wireOp",EDGE,"E6.0.4.23"),sQuery(id+"F0.wireOp",EDGE,"E6.0.4.24"),sQuery(id+"F0.wireOp",EDGE,"E6.0.4.25"),sQuery(id+"F0.wireOp",EDGE,"E6.0.4.26"),sQuery(id+"F0.wireOp",EDGE,"E6.0.4.27"),sQuery(id+"F0.wireOp",EDGE,"E6.0.4.28"),sQuery(id+"F0.wireOp",EDGE,"E6.0.4.29"),sQuery(id+"F0.wireOp",EDGE,"E6.0.4.30"),sQuery(id+"F0.wireOp",EDGE,"E6.0.4.31"),sQuery(id+"F0.wireOp",EDGE,"E6.0.4.33"),sQuery(id+"F0.wireOp",EDGE,"E6.0.4.34"),sQuery(id+"F0.wireOp",EDGE,"E6.0.4.36"),sQuery(id+"F0.wireOp",EDGE,"E6.0.4.37"),sQuery(id+"F0.wireOp",EDGE,"E6.0.4.38"),sQuery(id+"F0.wireOp",EDGE,"E6.0.4.39"),sQuery(id+"F0.wireOp",EDGE,"E6.0.4.41"),sQuery(id+"F0.wireOp",EDGE,"E6.0.4.42"),sQuery(id+"F0.wireOp",EDGE,"E6.0.4.43"),sQuery(id+"F0.wireOp",EDGE,"E6.0.4.44"),sQuery(id+"F0.wireOp",EDGE,"E6.0.4.46"),sQuery(id+"F0.wireOp",EDGE,"E6.0.4.48"),sQuery(id+"F0.wireOp",EDGE,"E6.0.4.49"),sQuery(id+"F0.wireOp",EDGE,"E6.0.4.51"),sQuery(id+"F0.wireOp",EDGE,"E6.0.4.52"),sQuery(id+"F0.wireOp",EDGE,"E6.0.4.53"),sQuery(id+"F0.wireOp",EDGE,"E6.0.4.54"),sQuery(id+"F0.wireOp",EDGE,"E6.0.4.55"),sQuery(id+"F0.wireOp",EDGE,"E6.0.4.57"),sQuery(id+"F0.wireOp",EDGE,"E6.0.4.59"),sQuery(id+"F0.wireOp",EDGE,"E6.0.4.60"),sQuery(id+"F0.wireOp",EDGE,"E6.0.4.62"),sQuery(id+"F0.wireOp",EDGE,"E6.0.4.63"),sQuery(id+"F0.wireOp",EDGE,"E6.0.4.64"),sQuery(id+"F0.wireOp",EDGE,"E6.0.4.65"),sQuery(id+"F0.wireOp",EDGE,"E6.0.4.66"),sQuery(id+"F0.wireOp",EDGE,"E6.0.4.67"),sQuery(id+"F0.wireOp",EDGE,"E6.0.4.68"),sQuery(id+"F0.wireOp",EDGE,"E6.0.4.70"),sQuery(id+"F0.wireOp",EDGE,"E6.0.4.71"),sQuery(id+"F0.wireOp",EDGE,"E6.0.4.72"),sQuery(id+"F0.wireOp",EDGE,"E6.0.4.73"),sQuery(id+"F0.wireOp",EDGE,"E6.0.4.75"),sQuery(id+"F0.wireOp",EDGE,"E6.0.4.76"),sQuery(id+"F0.wireOp",EDGE,"E6.0.4.77"),sQuery(id+"F0.wireOp",EDGE,"E6.0.4.78"),sQuery(id+"F0.wireOp",EDGE,"E6.0.4.80"),sQuery(id+"F0.wireOp",EDGE,"E6.0.4.81"),sQuery(id+"F0.wireOp",EDGE,"E6.0.4.82"),sQuery(id+"F0.wireOp",EDGE,"E6.0.4.83"),sQuery(id+"F0.wireOp",EDGE,"E6.0.4.85"),sQuery(id+"F0.wireOp",EDGE,"E6.0.4.86"),sQuery(id+"F0.wireOp",EDGE,"E6.0.4.87"),sQuery(id+"F0.wireOp",EDGE,"E6.0.4.88"),sQuery(id+"F0.wireOp",EDGE,"E6.0.4.89"),sQuery(id+"F0.wireOp",EDGE,"E6.0.4.90"),sQuery(id+"F0.wireOp",EDGE,"E6.0.4.91"),sQuery(id+"F0.wireOp",EDGE,"E6.0.4.92"),sQuery(id+"F0.wireOp",EDGE,"E6.0.4.94"),sQuery(id+"F0.wireOp",EDGE,"E6.0.4.95"),sQuery(id+"F0.wireOp",EDGE,"E6.0.4.96"),sQuery(id+"F0.wireOp",EDGE,"E6.0.4.97"),sQuery(id+"F0.wireOp",EDGE,"E6.0.4.98"),sQuery(id+"F0.wireOp",EDGE,"E6.0.4.99"),sQuery(id+"F0.wireOp",EDGE,"E6.0.4.100"),sQuery(id+"F0.wireOp",EDGE,"E6.0.4.101"),sQuery(id+"F0.wireOp",EDGE,"E6.0.4.102"),sQuery(id+"F0.wireOp",EDGE,"E6.0.4.103"),sQuery(id+"F0.wireOp",EDGE,"E6.0.4.104"),sQuery(id+"F0.wireOp",EDGE,"E6.0.4.105"),sQuery(id+"F0.wireOp",EDGE,"E6.0.4.106"),sQuery(id+"F0.wireOp",EDGE,"E6.0.4.107"),sQuery(id+"F0.wireOp",EDGE,"E6.0.4.108"),sQuery(id+"F0.wireOp",EDGE,"E6.0.4.109"),sQuery(id+"F0.wireOp",EDGE,"E6.0.4.110"),sQuery(id+"F0.wireOp",EDGE,"E6.0.4.111"),sQuery(id+"F0.wireOp",EDGE,"E6.0.4.112"),sQuery(id+"F0.wireOp",EDGE,"E6.0.4.113"),sQuery(id+"F0.wireOp",EDGE,"E6.0.4.114"),sQuery(id+"F0.wireOp",EDGE,"E6.0.4.115"),sQuery(id+"F0.wireOp",EDGE,"E6.0.4.117"),sQuery(id+"F0.wireOp",EDGE,"E6.0.4.118"),sQuery(id+"F0.wireOp",EDGE,"E6.0.4.120"),sQuery(id+"F0.wireOp",EDGE,"E6.0.4.121"),sQuery(id+"F0.wireOp",EDGE,"E6.0.4.122"),sQuery(id+"F0.wireOp",EDGE,"E6.0.4.123"),sQuery(id+"F0.wireOp",EDGE,"E6.0.4.124"),sQuery(id+"F0.wireOp",EDGE,"E6.0.4.125"),sQuery(id+"F0.wireOp",EDGE,"E6.0.4.126"),sQuery(id+"F0.wireOp",EDGE,"E6.0.4.127"),sQuery(id+"F0.wireOp",EDGE,"E6.0.4.128"),sQuery(id+"F0.wireOp",EDGE,"E6.0.4.129"),sQuery(id+"F0.wireOp",EDGE,"E6.0.4.130"),sQuery(id+"F0.wireOp",EDGE,"E6.0.4.131"),sQuery(id+"F0.wireOp",EDGE,"E6.0.4.132"),sQuery(id+"F0.wireOp",EDGE,"E6.0.4.133"),sQuery(id+"F0.wireOp",EDGE,"E6.0.4.134"),sQuery(id+"F0.wireOp",EDGE,"E6.0.4.135"),sQuery(id+"F0.wireOp",EDGE,"E6.0.4.136"),sQuery(id+"F0.wireOp",EDGE,"E6.0.4.137"),sQuery(id+"F0.wireOp",EDGE,"E6.0.4.138"),sQuery(id+"F0.wireOp",EDGE,"E6.0.4.139"),sQuery(id+"F0.wireOp",EDGE,"E6.0.4.140"),sQuery(id+"F0.wireOp",EDGE,"E6.0.4.141"),sQuery(id+"F0.wireOp",EDGE,"E6.0.4.143"),sQuery(id+"F0.wireOp",EDGE,"E6.0.4.144"),sQuery(id+"F0.wireOp",EDGE,"E10.bottom"),sQuery(id+"F0.wireOp",EDGE,"E10.top"),sQuery(id+"F0.wireOp",EDGE,"E10.left"),sQuery(id+"F0.wireOp",EDGE,"E10.right")])]});
            var Q1;
            Q1=qCreatedBy(makeId("Front.planeOp"),FACE);
            mirror(context, id + "F3", {"entities" : qUnion([Q0]), "mirrorPlane" : qUnion([Q1])});
        }
    });
